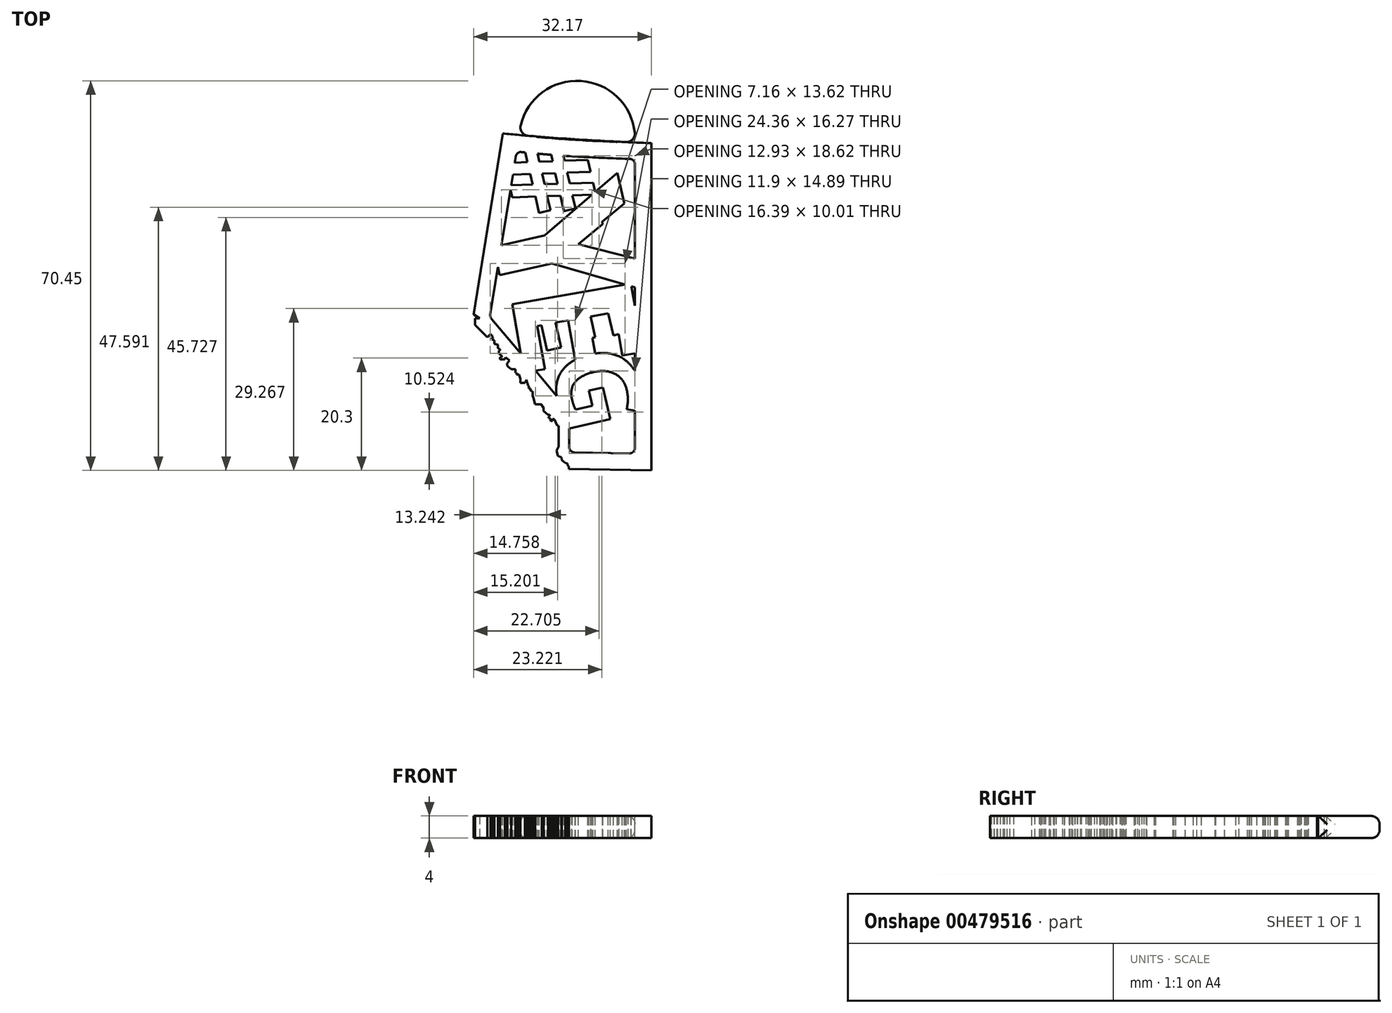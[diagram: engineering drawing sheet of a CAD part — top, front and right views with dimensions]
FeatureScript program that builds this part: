
annotation { "Feature Type Name" : "Feature", "Feature Type Description" : "" }
export const myFeature = defineFeature(function(context is Context, id is Id, definition is map)
    precondition{}
    {
        {
            var Q0;
            Q0=qCreatedBy(makeId("Top.planeOp"),FACE);
            var sketch = newSketch(context, id + "F0", { "sketchPlane" : qUnion([Q0])});
            skLineSegment(sketch, "E0", {"start": v(12.94, 76.8) * mm, "end": v(7.68, 44.1) * mm});
            skLineSegment(sketch, "E1", {"start": v(7.68, 44.1) * mm, "end": v(8.75, 43.35) * mm});
            skLineSegment(sketch, "E2", {"start": v(8.75, 43.35) * mm, "end": v(7.97, 43.35) * mm});
            skLineSegment(sketch, "E3", {"start": v(7.97, 43.35) * mm, "end": v(7.97, 42.17) * mm});
            skLineSegment(sketch, "E4", {"start": v(7.97, 42.17) * mm, "end": v(10.17, 39.93) * mm});
            skLineSegment(sketch, "E5", {"start": v(10.17, 39.93) * mm, "end": v(10.74, 40.49) * mm});
            skLineSegment(sketch, "E6", {"start": v(10.74, 40.49) * mm, "end": v(11.19, 40.03) * mm});
            skLineSegment(sketch, "E7", {"start": v(11.19, 40.03) * mm, "end": v(11, 39.57) * mm});
            skLineSegment(sketch, "E8", {"start": v(11, 39.57) * mm, "end": v(11.46, 39.39) * mm});
            skLineSegment(sketch, "E9", {"start": v(11.46, 39.39) * mm, "end": v(11.46, 38.73) * mm});
            skLineSegment(sketch, "E10", {"start": v(11.46, 38.73) * mm, "end": v(12.08, 38.61) * mm});
            skLineSegment(sketch, "E11", {"start": v(12.08, 38.61) * mm, "end": v(12.08, 37.96) * mm});
            skLineSegment(sketch, "E12", {"start": v(12.08, 37.96) * mm, "end": v(12.25, 37.87) * mm});
            skLineSegment(sketch, "E13", {"start": v(12.25, 37.87) * mm, "end": v(12.46, 37.8) * mm});
            skLineSegment(sketch, "E14", {"start": v(12.46, 37.8) * mm, "end": v(12.46, 37.52) * mm});
            skLineSegment(sketch, "E15", {"start": v(12.46, 37.52) * mm, "end": v(12.25, 37.52) * mm});
            skLineSegment(sketch, "E16", {"start": v(12.25, 37.52) * mm, "end": v(12.25, 36.96) * mm});
            skLineSegment(sketch, "E17", {"start": v(12.25, 36.96) * mm, "end": v(12.43, 36.93) * mm});
            skLineSegment(sketch, "E18", {"start": v(12.43, 36.93) * mm, "end": v(12.75, 36.55) * mm});
            skLineSegment(sketch, "E19", {"start": v(12.75, 36.55) * mm, "end": v(12.75, 36.3) * mm});
            skLineSegment(sketch, "E20", {"start": v(12.75, 36.3) * mm, "end": v(12.46, 36.3) * mm});
            skLineSegment(sketch, "E21", {"start": v(12.46, 36.3) * mm, "end": v(12.46, 35.94) * mm});
            skLineSegment(sketch, "E22", {"start": v(12.46, 35.94) * mm, "end": v(13.34, 35.94) * mm});
            skLineSegment(sketch, "E23", {"start": v(13.34, 35.94) * mm, "end": v(13.45, 36.34) * mm});
            skLineSegment(sketch, "E24", {"start": v(13.45, 36.34) * mm, "end": v(14.19, 35.72) * mm});
            skLineSegment(sketch, "E25", {"start": v(14.19, 35.72) * mm, "end": v(13.73, 35.19) * mm});
            skLineSegment(sketch, "E26", {"start": v(13.73, 35.19) * mm, "end": v(13.79, 34.75) * mm});
            skLineSegment(sketch, "E27", {"start": v(13.79, 34.75) * mm, "end": v(14.47, 34.2) * mm});
            skLineSegment(sketch, "E28", {"start": v(14.47, 34.2) * mm, "end": v(15.28, 34.2) * mm});
            skLineSegment(sketch, "E29", {"start": v(15.28, 34.2) * mm, "end": v(15.28, 33.54) * mm});
            skLineSegment(sketch, "E30", {"start": v(15.28, 33.54) * mm, "end": v(15.46, 33.54) * mm});
            skLineSegment(sketch, "E31", {"start": v(15.46, 33.54) * mm, "end": v(15.46, 33.22) * mm});
            skLineSegment(sketch, "E32", {"start": v(15.46, 33.22) * mm, "end": v(15.87, 33.22) * mm});
            skLineSegment(sketch, "E33", {"start": v(15.87, 33.22) * mm, "end": v(16.14, 32.43) * mm});
            skLineSegment(sketch, "E34", {"start": v(16.14, 32.43) * mm, "end": v(16.14, 31.7) * mm});
            skLineSegment(sketch, "E35", {"start": v(16.14, 31.7) * mm, "end": v(16.97, 31.7) * mm});
            skLineSegment(sketch, "E36", {"start": v(16.97, 31.7) * mm, "end": v(17.27, 32.23) * mm});
            skLineSegment(sketch, "E37", {"start": v(17.27, 32.23) * mm, "end": v(17.33, 31.74) * mm});
            skLineSegment(sketch, "E38", {"start": v(17.33, 31.74) * mm, "end": v(17.48, 31.65) * mm});
            skLineSegment(sketch, "E39", {"start": v(17.48, 31.65) * mm, "end": v(17.48, 31.25) * mm});
            skLineSegment(sketch, "E40", {"start": v(17.48, 31.25) * mm, "end": v(17.7, 31.18) * mm});
            skLineSegment(sketch, "E41", {"start": v(17.7, 31.18) * mm, "end": v(17.7, 30.7) * mm});
            skLineSegment(sketch, "E42", {"start": v(17.7, 30.7) * mm, "end": v(18.01, 30.66) * mm});
            skLineSegment(sketch, "E43", {"start": v(18.01, 30.66) * mm, "end": v(18.01, 30.29) * mm});
            skLineSegment(sketch, "E44", {"start": v(18.01, 30.29) * mm, "end": v(18.18, 30.2) * mm});
            skLineSegment(sketch, "E45", {"start": v(18.18, 30.2) * mm, "end": v(18.33, 30.17) * mm});
            skLineSegment(sketch, "E46", {"start": v(18.33, 30.17) * mm, "end": v(18.33, 29.33) * mm});
            skLineSegment(sketch, "E47", {"start": v(18.33, 29.33) * mm, "end": v(18.46, 29) * mm});
            skLineSegment(sketch, "E48", {"start": v(18.46, 29) * mm, "end": v(18.83, 27.8) * mm});
            skLineSegment(sketch, "E49", {"start": v(18.83, 27.8) * mm, "end": v(20, 27.8) * mm});
            skLineSegment(sketch, "E50", {"start": v(20, 27.8) * mm, "end": v(20, 27.5) * mm});
            skLineSegment(sketch, "E51", {"start": v(20, 27.5) * mm, "end": v(20.36, 27.3) * mm});
            skLineSegment(sketch, "E52", {"start": v(20.36, 27.3) * mm, "end": v(20.36, 26.6) * mm});
            skLineSegment(sketch, "E53", {"start": v(20.36, 26.6) * mm, "end": v(21.15, 25.9) * mm});
            skLineSegment(sketch, "E54", {"start": v(21.15, 25.9) * mm, "end": v(21.45, 25.9) * mm});
            skLineSegment(sketch, "E55", {"start": v(21.45, 25.9) * mm, "end": v(21.5, 25.75) * mm});
            skLineSegment(sketch, "E56", {"start": v(21.5, 25.75) * mm, "end": v(21.21, 25.6) * mm});
            skLineSegment(sketch, "E57", {"start": v(21.21, 25.6) * mm, "end": v(21.3, 25.31) * mm});
            skLineSegment(sketch, "E58", {"start": v(21.3, 25.31) * mm, "end": v(21.54, 25.28) * mm});
            skLineSegment(sketch, "E59", {"start": v(21.54, 25.28) * mm, "end": v(21.6, 24.78) * mm});
            skLineSegment(sketch, "E60", {"start": v(21.6, 24.78) * mm, "end": v(21.94, 24.82) * mm});
            skLineSegment(sketch, "E61", {"start": v(21.94, 24.82) * mm, "end": v(21.99, 25.2) * mm});
            skLineSegment(sketch, "E62", {"start": v(21.99, 25.2) * mm, "end": v(22.33, 25.1) * mm});
            skLineSegment(sketch, "E63", {"start": v(22.33, 25.1) * mm, "end": v(22.84, 23.96) * mm});
            skLineSegment(sketch, "E64", {"start": v(22.84, 23.96) * mm, "end": v(23.05, 23.94) * mm});
            skLineSegment(sketch, "E65", {"start": v(23.05, 23.94) * mm, "end": v(23.05, 22.88) * mm});
            skLineSegment(sketch, "E66", {"start": v(23.05, 22.88) * mm, "end": v(23.05, 20.17) * mm});
            skLineSegment(sketch, "E67", {"start": v(23.05, 20.17) * mm, "end": v(22.65, 19.46) * mm});
            skLineSegment(sketch, "E68", {"start": v(22.65, 19.46) * mm, "end": v(22.95, 18.48) * mm});
            skLineSegment(sketch, "E69", {"start": v(22.95, 18.48) * mm, "end": v(23.56, 18.23) * mm});
            skLineSegment(sketch, "E70", {"start": v(23.56, 18.23) * mm, "end": v(23.64, 17.74) * mm});
            skLineSegment(sketch, "E71", {"start": v(23.64, 17.74) * mm, "end": v(24.27, 17.22) * mm});
            skLineSegment(sketch, "E72", {"start": v(24.27, 17.22) * mm, "end": v(24.63, 17.14) * mm});
            skLineSegment(sketch, "E73", {"start": v(24.63, 17.14) * mm, "end": v(24.72, 16.67) * mm});
            skLineSegment(sketch, "E74", {"start": v(24.72, 16.67) * mm, "end": v(24.9, 16.57) * mm});
            skLineSegment(sketch, "E75", {"start": v(24.9, 16.57) * mm, "end": v(24.9, 16.14) * mm});
            skLineSegment(sketch, "E76", {"start": v(24.9, 16.14) * mm, "end": v(39.85, 15.87) * mm});
            skLineSegment(sketch, "E77", {"start": v(39.85, 15.87) * mm, "end": v(39.85, 75.04) * mm});
            skFitSpline(sketch, "E78", {"points": [v(12.94, 76.8) * mm, v(39.85, 75.04) * mm], "startDerivative": vector(26.48, -2.57) * mm, "endDerivative": vector(26.93, -1.05) * mm});
            skLineSegment(sketch, "E79.0", {"start": v(15.31, 72.63) * mm, "end": v(10.71, 44.07) * mm});
            skFitSpline(sketch, "E80.0", {"points": [v(12.65, 73.81) * mm, v(21.55, 72.95) * mm, v(30.71, 72.4) * mm, v(39.73, 72.04) * mm]});
            skLineSegment(sketch, "E81.0", {"start": v(25.93, 19.12) * mm, "end": v(35.83, 18.95) * mm});
            skLineSegment(sketch, "E82.trimOffspring", {"start": v(36.85, 19.95) * mm, "end": v(36.85, 71.2) * mm});
            skLineSegment(sketch, "E83", {"start": v(24.95, 20.12) * mm, "end": v(24.95, 26.3) * mm});
            skLineSegment(sketch, "E84", {"start": v(24.72, 26.95) * mm, "end": v(10.93, 43.26) * mm});
            skPoint(sketch, "E85.visualSharp", {"position": v(15.46, 73.55) * mm});
            skArc(sketch, "E85.filletArc", {"start": v(16.38, 73.47) * mm, "mid": v(15.68, 73.26) * mm, "end": v(15.31, 72.63) * mm});
            skPoint(sketch, "E86.visualSharp", {"position": v(36.85, 72.16) * mm});
            skArc(sketch, "E86.filletArc", {"start": v(36.85, 71.2) * mm, "mid": v(36.57, 71.9) * mm, "end": v(35.9, 72.2) * mm});
            skPoint(sketch, "E87.visualSharp", {"position": v(36.85, 18.93) * mm});
            skArc(sketch, "E87.filletArc", {"start": v(35.83, 18.95) * mm, "mid": v(36.55, 19.23) * mm, "end": v(36.85, 19.95) * mm});
            skPoint(sketch, "E88.visualSharp", {"position": v(24.95, 19.14) * mm});
            skArc(sketch, "E88.filletArc", {"start": v(24.95, 20.12) * mm, "mid": v(25.24, 19.42) * mm, "end": v(25.93, 19.12) * mm});
            skPoint(sketch, "E89.visualSharp", {"position": v(24.95, 26.67) * mm});
            skArc(sketch, "E89.filletArc", {"start": v(24.95, 26.3) * mm, "mid": v(24.9, 26.64) * mm, "end": v(24.72, 26.95) * mm});
            skPoint(sketch, "E90.visualSharp", {"position": v(10.64, 43.62) * mm});
            skArc(sketch, "E90.filletArc", {"start": v(10.71, 44.07) * mm, "mid": v(10.73, 43.64) * mm, "end": v(10.93, 43.26) * mm});
            skSolve(sketch);
        }
        {
            var Q0;
            Q0=makeQuery(id+"F0.imprint","IMPRINT",FACE,{"disambiguationData":[TD([[makeQuery(id+"F0.imprint","IMPRINT",EDGE,{"derivedFrom":sQuery(id+"F0.wireOp",EDGE,"E0")}),1.0]])]});
            extrude(context, id + "F1", {"entities" : qUnion([Q0]), "depth" : 4 * mm});
        }
        {
            var Q0;
            Q0=makeQuery(id+"F1.opExtrude","CAP_FACE",FACE,{"disambiguationData":[OSD([sQuery(id+"F0.wireOp",EDGE,"E0"),sQuery(id+"F0.wireOp",EDGE,"E1"),sQuery(id+"F0.wireOp",EDGE,"E2"),sQuery(id+"F0.wireOp",EDGE,"E3"),sQuery(id+"F0.wireOp",EDGE,"E4"),sQuery(id+"F0.wireOp",EDGE,"E5"),sQuery(id+"F0.wireOp",EDGE,"E6"),sQuery(id+"F0.wireOp",EDGE,"E7"),sQuery(id+"F0.wireOp",EDGE,"E8"),sQuery(id+"F0.wireOp",EDGE,"E9"),sQuery(id+"F0.wireOp",EDGE,"E10"),sQuery(id+"F0.wireOp",EDGE,"E11"),sQuery(id+"F0.wireOp",EDGE,"E12"),sQuery(id+"F0.wireOp",EDGE,"E13"),sQuery(id+"F0.wireOp",EDGE,"E14"),sQuery(id+"F0.wireOp",EDGE,"E15"),sQuery(id+"F0.wireOp",EDGE,"E16"),sQuery(id+"F0.wireOp",EDGE,"E17"),sQuery(id+"F0.wireOp",EDGE,"E18"),sQuery(id+"F0.wireOp",EDGE,"E19"),sQuery(id+"F0.wireOp",EDGE,"E20"),sQuery(id+"F0.wireOp",EDGE,"E21"),sQuery(id+"F0.wireOp",EDGE,"E22"),sQuery(id+"F0.wireOp",EDGE,"E23"),sQuery(id+"F0.wireOp",EDGE,"E24"),sQuery(id+"F0.wireOp",EDGE,"E25"),sQuery(id+"F0.wireOp",EDGE,"E26"),sQuery(id+"F0.wireOp",EDGE,"E27"),sQuery(id+"F0.wireOp",EDGE,"E28"),sQuery(id+"F0.wireOp",EDGE,"E29"),sQuery(id+"F0.wireOp",EDGE,"E30"),sQuery(id+"F0.wireOp",EDGE,"E31"),sQuery(id+"F0.wireOp",EDGE,"E32"),sQuery(id+"F0.wireOp",EDGE,"E33"),sQuery(id+"F0.wireOp",EDGE,"E34"),sQuery(id+"F0.wireOp",EDGE,"E35"),sQuery(id+"F0.wireOp",EDGE,"E36"),sQuery(id+"F0.wireOp",EDGE,"E37"),sQuery(id+"F0.wireOp",EDGE,"E38"),sQuery(id+"F0.wireOp",EDGE,"E39"),sQuery(id+"F0.wireOp",EDGE,"E40"),sQuery(id+"F0.wireOp",EDGE,"E41"),sQuery(id+"F0.wireOp",EDGE,"E42"),sQuery(id+"F0.wireOp",EDGE,"E43"),sQuery(id+"F0.wireOp",EDGE,"E44"),sQuery(id+"F0.wireOp",EDGE,"E45"),sQuery(id+"F0.wireOp",EDGE,"E46"),sQuery(id+"F0.wireOp",EDGE,"E47"),sQuery(id+"F0.wireOp",EDGE,"E48"),sQuery(id+"F0.wireOp",EDGE,"E49"),sQuery(id+"F0.wireOp",EDGE,"E50"),sQuery(id+"F0.wireOp",EDGE,"E51"),sQuery(id+"F0.wireOp",EDGE,"E52"),sQuery(id+"F0.wireOp",EDGE,"E53"),sQuery(id+"F0.wireOp",EDGE,"E54"),sQuery(id+"F0.wireOp",EDGE,"E55"),sQuery(id+"F0.wireOp",EDGE,"E56"),sQuery(id+"F0.wireOp",EDGE,"E57"),sQuery(id+"F0.wireOp",EDGE,"E58"),sQuery(id+"F0.wireOp",EDGE,"E59"),sQuery(id+"F0.wireOp",EDGE,"E60"),sQuery(id+"F0.wireOp",EDGE,"E61"),sQuery(id+"F0.wireOp",EDGE,"E62"),sQuery(id+"F0.wireOp",EDGE,"E63"),sQuery(id+"F0.wireOp",EDGE,"E64"),sQuery(id+"F0.wireOp",EDGE,"E65"),sQuery(id+"F0.wireOp",EDGE,"E66"),sQuery(id+"F0.wireOp",EDGE,"E67"),sQuery(id+"F0.wireOp",EDGE,"E68"),sQuery(id+"F0.wireOp",EDGE,"E69"),sQuery(id+"F0.wireOp",EDGE,"E70"),sQuery(id+"F0.wireOp",EDGE,"E71"),sQuery(id+"F0.wireOp",EDGE,"E72"),sQuery(id+"F0.wireOp",EDGE,"E73"),sQuery(id+"F0.wireOp",EDGE,"E74"),sQuery(id+"F0.wireOp",EDGE,"E75"),sQuery(id+"F0.wireOp",EDGE,"E76"),sQuery(id+"F0.wireOp",EDGE,"E77"),sQuery(id+"F0.wireOp",EDGE,"E78"),sQuery(id+"F0.wireOp",EDGE,"E79.0"),sQuery(id+"F0.wireOp",EDGE,"E80.0"),sQuery(id+"F0.wireOp",EDGE,"E81.0"),sQuery(id+"F0.wireOp",EDGE,"E82.trimOffspring"),sQuery(id+"F0.wireOp",EDGE,"E83"),sQuery(id+"F0.wireOp",EDGE,"E84"),sQuery(id+"F0.wireOp",EDGE,"E85.filletArc"),sQuery(id+"F0.wireOp",EDGE,"E86.filletArc"),sQuery(id+"F0.wireOp",EDGE,"E87.filletArc"),sQuery(id+"F0.wireOp",EDGE,"E88.filletArc"),sQuery(id+"F0.wireOp",EDGE,"E89.filletArc"),sQuery(id+"F0.wireOp",EDGE,"E90.filletArc")])],"isStart":false});
            var sketch = newSketch(context, id + "F2", { "sketchPlane" : qUnion([Q0])});
            skText(sketch, "E91", { "text": "#YEG", "fontName": "NotoSans-Bold.ttf"});
            const initialGuessF2  = {"E91": [0.01276, 0.07352, 0.22255, -0.97492, 0.015]};
            skSetInitialGuess(sketch, initialGuessF2);
            skSolve(sketch);
        }
        {
            var Q0;
            Q0=makeQuery(id+"F2.imprint","IMPRINT",FACE,{"disambiguationData":[TD([[makeQuery(id+"F2.imprint","IMPRINT",EDGE,{"derivedFrom":sQuery(id+"F2.wireOp",EDGE,"E91.sketch_text.stroke-0")}),-1.0]])]});
            var Q1;
            Q1=makeQuery(id+"F2.imprint","IMPRINT",FACE,{"disambiguationData":[TD([[makeQuery(id+"F2.imprint","IMPRINT",EDGE,{"derivedFrom":sQuery(id+"F2.wireOp",EDGE,"E91.sketch_text.stroke-32")}),-1.0]])]});
            var Q2;
            Q2=makeQuery(id+"F2.imprint","IMPRINT",FACE,{"disambiguationData":[TD([[makeQuery(id+"F2.imprint","IMPRINT",EDGE,{"derivedFrom":sQuery(id+"F2.wireOp",EDGE,"E91.sketch_text.stroke-41")}),-1.0]])]});
            var Q3;
            Q3=makeQuery(id+"F2.imprint","IMPRINT",FACE,{"disambiguationData":[TD([[makeQuery(id+"F2.imprint","IMPRINT",EDGE,{"derivedFrom":sQuery(id+"F2.wireOp",EDGE,"E91.sketch_text.stroke-53")}),-1.0]])]});
            var Q4;
            Q4=makeQuery(id+"F1.opExtrude","CAP_FACE",FACE,{"disambiguationData":[OSD([sQuery(id+"F0.wireOp",EDGE,"E0"),sQuery(id+"F0.wireOp",EDGE,"E1"),sQuery(id+"F0.wireOp",EDGE,"E2"),sQuery(id+"F0.wireOp",EDGE,"E3"),sQuery(id+"F0.wireOp",EDGE,"E4"),sQuery(id+"F0.wireOp",EDGE,"E5"),sQuery(id+"F0.wireOp",EDGE,"E6"),sQuery(id+"F0.wireOp",EDGE,"E7"),sQuery(id+"F0.wireOp",EDGE,"E8"),sQuery(id+"F0.wireOp",EDGE,"E9"),sQuery(id+"F0.wireOp",EDGE,"E10"),sQuery(id+"F0.wireOp",EDGE,"E11"),sQuery(id+"F0.wireOp",EDGE,"E12"),sQuery(id+"F0.wireOp",EDGE,"E13"),sQuery(id+"F0.wireOp",EDGE,"E14"),sQuery(id+"F0.wireOp",EDGE,"E15"),sQuery(id+"F0.wireOp",EDGE,"E16"),sQuery(id+"F0.wireOp",EDGE,"E17"),sQuery(id+"F0.wireOp",EDGE,"E18"),sQuery(id+"F0.wireOp",EDGE,"E19"),sQuery(id+"F0.wireOp",EDGE,"E20"),sQuery(id+"F0.wireOp",EDGE,"E21"),sQuery(id+"F0.wireOp",EDGE,"E22"),sQuery(id+"F0.wireOp",EDGE,"E23"),sQuery(id+"F0.wireOp",EDGE,"E24"),sQuery(id+"F0.wireOp",EDGE,"E25"),sQuery(id+"F0.wireOp",EDGE,"E26"),sQuery(id+"F0.wireOp",EDGE,"E27"),sQuery(id+"F0.wireOp",EDGE,"E28"),sQuery(id+"F0.wireOp",EDGE,"E29"),sQuery(id+"F0.wireOp",EDGE,"E30"),sQuery(id+"F0.wireOp",EDGE,"E31"),sQuery(id+"F0.wireOp",EDGE,"E32"),sQuery(id+"F0.wireOp",EDGE,"E33"),sQuery(id+"F0.wireOp",EDGE,"E34"),sQuery(id+"F0.wireOp",EDGE,"E35"),sQuery(id+"F0.wireOp",EDGE,"E36"),sQuery(id+"F0.wireOp",EDGE,"E37"),sQuery(id+"F0.wireOp",EDGE,"E38"),sQuery(id+"F0.wireOp",EDGE,"E39"),sQuery(id+"F0.wireOp",EDGE,"E40"),sQuery(id+"F0.wireOp",EDGE,"E41"),sQuery(id+"F0.wireOp",EDGE,"E42"),sQuery(id+"F0.wireOp",EDGE,"E43"),sQuery(id+"F0.wireOp",EDGE,"E44"),sQuery(id+"F0.wireOp",EDGE,"E45"),sQuery(id+"F0.wireOp",EDGE,"E46"),sQuery(id+"F0.wireOp",EDGE,"E47"),sQuery(id+"F0.wireOp",EDGE,"E48"),sQuery(id+"F0.wireOp",EDGE,"E49"),sQuery(id+"F0.wireOp",EDGE,"E50"),sQuery(id+"F0.wireOp",EDGE,"E51"),sQuery(id+"F0.wireOp",EDGE,"E52"),sQuery(id+"F0.wireOp",EDGE,"E53"),sQuery(id+"F0.wireOp",EDGE,"E54"),sQuery(id+"F0.wireOp",EDGE,"E55"),sQuery(id+"F0.wireOp",EDGE,"E56"),sQuery(id+"F0.wireOp",EDGE,"E57"),sQuery(id+"F0.wireOp",EDGE,"E58"),sQuery(id+"F0.wireOp",EDGE,"E59"),sQuery(id+"F0.wireOp",EDGE,"E60"),sQuery(id+"F0.wireOp",EDGE,"E61"),sQuery(id+"F0.wireOp",EDGE,"E62"),sQuery(id+"F0.wireOp",EDGE,"E63"),sQuery(id+"F0.wireOp",EDGE,"E64"),sQuery(id+"F0.wireOp",EDGE,"E65"),sQuery(id+"F0.wireOp",EDGE,"E66"),sQuery(id+"F0.wireOp",EDGE,"E67"),sQuery(id+"F0.wireOp",EDGE,"E68"),sQuery(id+"F0.wireOp",EDGE,"E69"),sQuery(id+"F0.wireOp",EDGE,"E70"),sQuery(id+"F0.wireOp",EDGE,"E71"),sQuery(id+"F0.wireOp",EDGE,"E72"),sQuery(id+"F0.wireOp",EDGE,"E73"),sQuery(id+"F0.wireOp",EDGE,"E74"),sQuery(id+"F0.wireOp",EDGE,"E75"),sQuery(id+"F0.wireOp",EDGE,"E76"),sQuery(id+"F0.wireOp",EDGE,"E77"),sQuery(id+"F0.wireOp",EDGE,"E78"),sQuery(id+"F0.wireOp",EDGE,"E79.0"),sQuery(id+"F0.wireOp",EDGE,"E80.0"),sQuery(id+"F0.wireOp",EDGE,"E81.0"),sQuery(id+"F0.wireOp",EDGE,"E82.trimOffspring"),sQuery(id+"F0.wireOp",EDGE,"E83"),sQuery(id+"F0.wireOp",EDGE,"E84"),sQuery(id+"F0.wireOp",EDGE,"E85.filletArc"),sQuery(id+"F0.wireOp",EDGE,"E86.filletArc"),sQuery(id+"F0.wireOp",EDGE,"E87.filletArc"),sQuery(id+"F0.wireOp",EDGE,"E88.filletArc"),sQuery(id+"F0.wireOp",EDGE,"E89.filletArc"),sQuery(id+"F0.wireOp",EDGE,"E90.filletArc")])],"isStart":true});
            extrude(context, id + "F3", {"entities" : qUnion([Q0, Q1, Q2, Q3]), "endBound" : BoundingType.UP_TO_SURFACE, "oppositeDirection" : true, "endBoundEntityFace" : qUnion([Q4]), "depth" : 25 * mm});
        }
        {
            var Q0;
            Q0=makeQuery(id+"F3.opExtrude","SWEPT_BODY",BODY,{"disambiguationData":[OSD([sQuery(id+"F0.wireOp",EDGE,"E79.0"),sQuery(id+"F0.wireOp",EDGE,"E80.0"),sQuery(id+"F2.wireOp",EDGE,"E91.sketch_text.stroke-0"),sQuery(id+"F2.wireOp",EDGE,"E91.sketch_text.stroke-1"),sQuery(id+"F2.wireOp",EDGE,"E91.sketch_text.stroke-2"),sQuery(id+"F2.wireOp",EDGE,"E91.sketch_text.stroke-3"),sQuery(id+"F2.wireOp",EDGE,"E91.sketch_text.stroke-4"),sQuery(id+"F2.wireOp",EDGE,"E91.sketch_text.stroke-5"),sQuery(id+"F2.wireOp",EDGE,"E91.sketch_text.stroke-6"),sQuery(id+"F2.wireOp",EDGE,"E91.sketch_text.stroke-7"),sQuery(id+"F2.wireOp",EDGE,"E91.sketch_text.stroke-8"),sQuery(id+"F2.wireOp",EDGE,"E91.sketch_text.stroke-10"),sQuery(id+"F2.wireOp",EDGE,"E91.sketch_text.stroke-11"),sQuery(id+"F2.wireOp",EDGE,"E91.sketch_text.stroke-13"),sQuery(id+"F2.wireOp",EDGE,"E91.sketch_text.stroke-14"),sQuery(id+"F2.wireOp",EDGE,"E91.sketch_text.stroke-15"),sQuery(id+"F2.wireOp",EDGE,"E91.sketch_text.stroke-17"),sQuery(id+"F2.wireOp",EDGE,"E91.sketch_text.stroke-18"),sQuery(id+"F2.wireOp",EDGE,"E91.sketch_text.stroke-19"),sQuery(id+"F2.wireOp",EDGE,"E91.sketch_text.stroke-20"),sQuery(id+"F2.wireOp",EDGE,"E91.sketch_text.stroke-21"),sQuery(id+"F2.wireOp",EDGE,"E91.sketch_text.stroke-22"),sQuery(id+"F2.wireOp",EDGE,"E91.sketch_text.stroke-23"),sQuery(id+"F2.wireOp",EDGE,"E91.sketch_text.stroke-24"),sQuery(id+"F2.wireOp",EDGE,"E91.sketch_text.stroke-25"),sQuery(id+"F2.wireOp",EDGE,"E91.sketch_text.stroke-26"),sQuery(id+"F2.wireOp",EDGE,"E91.sketch_text.stroke-27"),sQuery(id+"F2.wireOp",EDGE,"E91.sketch_text.stroke-28"),sQuery(id+"F2.wireOp",EDGE,"E91.sketch_text.stroke-29"),sQuery(id+"F2.wireOp",EDGE,"E91.sketch_text.stroke-30"),sQuery(id+"F2.wireOp",EDGE,"E91.sketch_text.stroke-31")])]});
            var Q1;
            Q1=makeQuery(id+"F1.opExtrude","SWEPT_BODY",BODY,{"disambiguationData":[OSD([sQuery(id+"F0.wireOp",EDGE,"E0"),sQuery(id+"F0.wireOp",EDGE,"E1"),sQuery(id+"F0.wireOp",EDGE,"E2"),sQuery(id+"F0.wireOp",EDGE,"E3"),sQuery(id+"F0.wireOp",EDGE,"E4"),sQuery(id+"F0.wireOp",EDGE,"E5"),sQuery(id+"F0.wireOp",EDGE,"E6"),sQuery(id+"F0.wireOp",EDGE,"E7"),sQuery(id+"F0.wireOp",EDGE,"E8"),sQuery(id+"F0.wireOp",EDGE,"E9"),sQuery(id+"F0.wireOp",EDGE,"E10"),sQuery(id+"F0.wireOp",EDGE,"E11"),sQuery(id+"F0.wireOp",EDGE,"E12"),sQuery(id+"F0.wireOp",EDGE,"E13"),sQuery(id+"F0.wireOp",EDGE,"E14"),sQuery(id+"F0.wireOp",EDGE,"E15"),sQuery(id+"F0.wireOp",EDGE,"E16"),sQuery(id+"F0.wireOp",EDGE,"E17"),sQuery(id+"F0.wireOp",EDGE,"E18"),sQuery(id+"F0.wireOp",EDGE,"E19"),sQuery(id+"F0.wireOp",EDGE,"E20"),sQuery(id+"F0.wireOp",EDGE,"E21"),sQuery(id+"F0.wireOp",EDGE,"E22"),sQuery(id+"F0.wireOp",EDGE,"E23"),sQuery(id+"F0.wireOp",EDGE,"E24"),sQuery(id+"F0.wireOp",EDGE,"E25"),sQuery(id+"F0.wireOp",EDGE,"E26"),sQuery(id+"F0.wireOp",EDGE,"E27"),sQuery(id+"F0.wireOp",EDGE,"E28"),sQuery(id+"F0.wireOp",EDGE,"E29"),sQuery(id+"F0.wireOp",EDGE,"E30"),sQuery(id+"F0.wireOp",EDGE,"E31"),sQuery(id+"F0.wireOp",EDGE,"E32"),sQuery(id+"F0.wireOp",EDGE,"E33"),sQuery(id+"F0.wireOp",EDGE,"E34"),sQuery(id+"F0.wireOp",EDGE,"E35"),sQuery(id+"F0.wireOp",EDGE,"E36"),sQuery(id+"F0.wireOp",EDGE,"E37"),sQuery(id+"F0.wireOp",EDGE,"E38"),sQuery(id+"F0.wireOp",EDGE,"E39"),sQuery(id+"F0.wireOp",EDGE,"E40"),sQuery(id+"F0.wireOp",EDGE,"E41"),sQuery(id+"F0.wireOp",EDGE,"E42"),sQuery(id+"F0.wireOp",EDGE,"E43"),sQuery(id+"F0.wireOp",EDGE,"E44"),sQuery(id+"F0.wireOp",EDGE,"E45"),sQuery(id+"F0.wireOp",EDGE,"E46"),sQuery(id+"F0.wireOp",EDGE,"E47"),sQuery(id+"F0.wireOp",EDGE,"E48"),sQuery(id+"F0.wireOp",EDGE,"E49"),sQuery(id+"F0.wireOp",EDGE,"E50"),sQuery(id+"F0.wireOp",EDGE,"E51"),sQuery(id+"F0.wireOp",EDGE,"E52"),sQuery(id+"F0.wireOp",EDGE,"E53"),sQuery(id+"F0.wireOp",EDGE,"E54"),sQuery(id+"F0.wireOp",EDGE,"E55"),sQuery(id+"F0.wireOp",EDGE,"E56"),sQuery(id+"F0.wireOp",EDGE,"E57"),sQuery(id+"F0.wireOp",EDGE,"E58"),sQuery(id+"F0.wireOp",EDGE,"E59"),sQuery(id+"F0.wireOp",EDGE,"E60"),sQuery(id+"F0.wireOp",EDGE,"E61"),sQuery(id+"F0.wireOp",EDGE,"E62"),sQuery(id+"F0.wireOp",EDGE,"E63"),sQuery(id+"F0.wireOp",EDGE,"E64"),sQuery(id+"F0.wireOp",EDGE,"E65"),sQuery(id+"F0.wireOp",EDGE,"E66"),sQuery(id+"F0.wireOp",EDGE,"E67"),sQuery(id+"F0.wireOp",EDGE,"E68"),sQuery(id+"F0.wireOp",EDGE,"E69"),sQuery(id+"F0.wireOp",EDGE,"E70"),sQuery(id+"F0.wireOp",EDGE,"E71"),sQuery(id+"F0.wireOp",EDGE,"E72"),sQuery(id+"F0.wireOp",EDGE,"E73"),sQuery(id+"F0.wireOp",EDGE,"E74"),sQuery(id+"F0.wireOp",EDGE,"E75"),sQuery(id+"F0.wireOp",EDGE,"E76"),sQuery(id+"F0.wireOp",EDGE,"E77"),sQuery(id+"F0.wireOp",EDGE,"E78"),sQuery(id+"F0.wireOp",EDGE,"E79.0"),sQuery(id+"F0.wireOp",EDGE,"E80.0"),sQuery(id+"F0.wireOp",EDGE,"E81.0"),sQuery(id+"F0.wireOp",EDGE,"E82.trimOffspring"),sQuery(id+"F0.wireOp",EDGE,"E83"),sQuery(id+"F0.wireOp",EDGE,"E84"),sQuery(id+"F0.wireOp",EDGE,"E85.filletArc"),sQuery(id+"F0.wireOp",EDGE,"E86.filletArc"),sQuery(id+"F0.wireOp",EDGE,"E87.filletArc"),sQuery(id+"F0.wireOp",EDGE,"E88.filletArc"),sQuery(id+"F0.wireOp",EDGE,"E89.filletArc"),sQuery(id+"F0.wireOp",EDGE,"E90.filletArc")])]});
            booleanBodies(context, id + "F4", {"operationType" : BooleanOperationType.UNION, "tools" : qUnion([Q0, Q1])});
        }
        {
            var Q0;
            Q0=makeQuery(id+"F3.opExtrude","SWEPT_BODY",BODY,{"disambiguationData":[OSD([sQuery(id+"F0.wireOp",EDGE,"E82.trimOffspring"),sQuery(id+"F0.wireOp",EDGE,"E83"),sQuery(id+"F0.wireOp",EDGE,"E84"),sQuery(id+"F0.wireOp",EDGE,"E89.filletArc"),sQuery(id+"F2.wireOp",EDGE,"E91.sketch_text.stroke-53"),sQuery(id+"F2.wireOp",EDGE,"E91.sketch_text.stroke-54"),sQuery(id+"F2.wireOp",EDGE,"E91.sketch_text.stroke-57"),sQuery(id+"F2.wireOp",EDGE,"E91.sketch_text.stroke-58"),sQuery(id+"F2.wireOp",EDGE,"E91.sketch_text.stroke-59"),sQuery(id+"F2.wireOp",EDGE,"E91.sketch_text.stroke-60"),sQuery(id+"F2.wireOp",EDGE,"E91.sketch_text.stroke-62"),sQuery(id+"F2.wireOp",EDGE,"E91.sketch_text.stroke-63"),sQuery(id+"F2.wireOp",EDGE,"E91.sketch_text.stroke-64"),sQuery(id+"F2.wireOp",EDGE,"E91.sketch_text.stroke-65"),sQuery(id+"F2.wireOp",EDGE,"E91.sketch_text.stroke-66"),sQuery(id+"F2.wireOp",EDGE,"E91.sketch_text.stroke-67"),sQuery(id+"F2.wireOp",EDGE,"E91.sketch_text.stroke-68"),sQuery(id+"F2.wireOp",EDGE,"E91.sketch_text.stroke-69"),sQuery(id+"F2.wireOp",EDGE,"E91.sketch_text.stroke-70"),sQuery(id+"F2.wireOp",EDGE,"E91.sketch_text.stroke-71")])]});
            var Q1;
            Q1=makeQuery(id+"F3.opExtrude","SWEPT_BODY",BODY,{"disambiguationData":[OSD([sQuery(id+"F0.wireOp",EDGE,"E79.0"),sQuery(id+"F0.wireOp",EDGE,"E80.0"),sQuery(id+"F2.wireOp",EDGE,"E91.sketch_text.stroke-0"),sQuery(id+"F2.wireOp",EDGE,"E91.sketch_text.stroke-1"),sQuery(id+"F2.wireOp",EDGE,"E91.sketch_text.stroke-2"),sQuery(id+"F2.wireOp",EDGE,"E91.sketch_text.stroke-3"),sQuery(id+"F2.wireOp",EDGE,"E91.sketch_text.stroke-4"),sQuery(id+"F2.wireOp",EDGE,"E91.sketch_text.stroke-5"),sQuery(id+"F2.wireOp",EDGE,"E91.sketch_text.stroke-6"),sQuery(id+"F2.wireOp",EDGE,"E91.sketch_text.stroke-7"),sQuery(id+"F2.wireOp",EDGE,"E91.sketch_text.stroke-8"),sQuery(id+"F2.wireOp",EDGE,"E91.sketch_text.stroke-10"),sQuery(id+"F2.wireOp",EDGE,"E91.sketch_text.stroke-11"),sQuery(id+"F2.wireOp",EDGE,"E91.sketch_text.stroke-13"),sQuery(id+"F2.wireOp",EDGE,"E91.sketch_text.stroke-14"),sQuery(id+"F2.wireOp",EDGE,"E91.sketch_text.stroke-15"),sQuery(id+"F2.wireOp",EDGE,"E91.sketch_text.stroke-17"),sQuery(id+"F2.wireOp",EDGE,"E91.sketch_text.stroke-18"),sQuery(id+"F2.wireOp",EDGE,"E91.sketch_text.stroke-19"),sQuery(id+"F2.wireOp",EDGE,"E91.sketch_text.stroke-20"),sQuery(id+"F2.wireOp",EDGE,"E91.sketch_text.stroke-21"),sQuery(id+"F2.wireOp",EDGE,"E91.sketch_text.stroke-22"),sQuery(id+"F2.wireOp",EDGE,"E91.sketch_text.stroke-23"),sQuery(id+"F2.wireOp",EDGE,"E91.sketch_text.stroke-24"),sQuery(id+"F2.wireOp",EDGE,"E91.sketch_text.stroke-25"),sQuery(id+"F2.wireOp",EDGE,"E91.sketch_text.stroke-26"),sQuery(id+"F2.wireOp",EDGE,"E91.sketch_text.stroke-27"),sQuery(id+"F2.wireOp",EDGE,"E91.sketch_text.stroke-28"),sQuery(id+"F2.wireOp",EDGE,"E91.sketch_text.stroke-29"),sQuery(id+"F2.wireOp",EDGE,"E91.sketch_text.stroke-30"),sQuery(id+"F2.wireOp",EDGE,"E91.sketch_text.stroke-31")])]});
            booleanBodies(context, id + "F5", {"operationType" : BooleanOperationType.UNION, "tools" : qUnion([Q0, Q1])});
        }
        {
            var Q0;
            Q0=makeQuery(id+"F3.opExtrude","SWEPT_FACE",FACE,{"disambiguationData":[OSD([sQuery(id+"F2.wireOp",EDGE,"E91.sketch_text.stroke-39")])]});
            var sketch = newSketch(context, id + "F6", { "sketchPlane" : qUnion([Q0])});
            skLineSegment(sketch, "E92.0.0", {"start": v(51.97, 4) * mm, "end": v(51.97, 0) * mm});
            skLineSegment(sketch, "E92.0.1", {"start": v(51.97, 0) * mm, "end": v(55.38, 0) * mm});
            skLineSegment(sketch, "E92.0.2", {"start": v(55.38, 0) * mm, "end": v(55.38, 4) * mm});
            skLineSegment(sketch, "E92.0.3", {"start": v(55.38, 4) * mm, "end": v(51.97, 4) * mm});
            skLineSegment(sketch, "E93.0", {"start": v(52.97, 3) * mm, "end": v(52.97, 1) * mm});
            skLineSegment(sketch, "E93.1", {"start": v(54.38, 3) * mm, "end": v(52.97, 3) * mm});
            skLineSegment(sketch, "E93.2", {"start": v(54.38, 1) * mm, "end": v(54.38, 3) * mm});
            skLineSegment(sketch, "E93.3", {"start": v(52.97, 1) * mm, "end": v(54.38, 1) * mm});
            skLineSegment(sketch, "E94", {"start": v(52.97, 1) * mm, "end": v(52.97, 0) * mm});
            skLineSegment(sketch, "E95", {"start": v(54.38, 1) * mm, "end": v(54.38, 0) * mm});
            skSolve(sketch);
        }
        {
            var Q0;
            Q0=makeQuery(id+"F6.imprint","IMPRINT",FACE,{"disambiguationData":[TD([[makeQuery(id+"F6.imprint","IMPRINT",EDGE,{"derivedFrom":sQuery(id+"F6.wireOp",EDGE,"E93.3")}),-1.0]])]});
            var Q1;
            {var subQ7=sQuery(id+"F0.wireOp",EDGE,"E86.filletArc");var subQ11=sQuery(id+"F0.wireOp",EDGE,"E82.trimOffspring");Q1=makeQuery(id+"F5.opBoolean","SPLIT",FACE,{"disambiguationData":[TD([makeQuery(id+"F1.opExtrude","SWEPT_FACE",FACE,{"disambiguationData":[OSD([subQ7])]})])],"derivedFrom":makeQuery(id+"F1.opExtrude","SWEPT_FACE",FACE,{"disambiguationData":[OSD([subQ11])]})});}
            extrude(context, id + "F7", {"entities" : qUnion([Q0]), "endBound" : BoundingType.UP_TO_SURFACE, "endBoundEntityFace" : qUnion([Q1]), "depth" : 25 * mm});
        }
        {
            var Q0;
            Q0=makeQuery(id+"F3.opExtrude","SWEPT_FACE",FACE,{"disambiguationData":[OSD([sQuery(id+"F2.wireOp",EDGE,"E91.sketch_text.stroke-33")])]});
            var sketch = newSketch(context, id + "F8", { "sketchPlane" : qUnion([Q0])});
            skLineSegment(sketch, "E96.0.0", {"start": v(42.38, 4) * mm, "end": v(42.38, 0) * mm});
            skLineSegment(sketch, "E96.0.1", {"start": v(42.38, 0) * mm, "end": v(45.78, 0) * mm});
            skLineSegment(sketch, "E96.0.2", {"start": v(45.78, 0) * mm, "end": v(45.78, 4) * mm});
            skLineSegment(sketch, "E96.0.3", {"start": v(45.78, 4) * mm, "end": v(42.38, 4) * mm});
            skLineSegment(sketch, "E97.0", {"start": v(43.38, 3) * mm, "end": v(43.38, 1) * mm});
            skLineSegment(sketch, "E97.1", {"start": v(44.78, 3) * mm, "end": v(43.38, 3) * mm});
            skLineSegment(sketch, "E97.2", {"start": v(44.78, 1) * mm, "end": v(44.78, 3) * mm});
            skLineSegment(sketch, "E97.3", {"start": v(43.38, 1) * mm, "end": v(44.78, 1) * mm});
            skLineSegment(sketch, "E98", {"start": v(43.38, 1) * mm, "end": v(43.38, 0) * mm});
            skLineSegment(sketch, "E99", {"start": v(44.78, 1) * mm, "end": v(44.78, 0) * mm});
            skSolve(sketch);
        }
        {
            var Q0;
            Q0=makeQuery(id+"F8.imprint","IMPRINT",FACE,{"disambiguationData":[TD([[makeQuery(id+"F8.imprint","IMPRINT",EDGE,{"derivedFrom":sQuery(id+"F8.wireOp",EDGE,"E97.3")}),-1.0]])]});
            var Q1;
            {var subQ7=sQuery(id+"F0.wireOp",EDGE,"E86.filletArc");var subQ11=sQuery(id+"F0.wireOp",EDGE,"E82.trimOffspring");Q1=makeQuery(id+"F5.opBoolean","SPLIT",FACE,{"disambiguationData":[TD([makeQuery(id+"F1.opExtrude","SWEPT_FACE",FACE,{"disambiguationData":[OSD([subQ7])]})])],"derivedFrom":makeQuery(id+"F1.opExtrude","SWEPT_FACE",FACE,{"disambiguationData":[OSD([subQ11])]})});}
            extrude(context, id + "F9", {"entities" : qUnion([Q0]), "endBound" : BoundingType.UP_TO_SURFACE, "endBoundEntityFace" : qUnion([Q1]), "depth" : 25 * mm});
        }
        {
            var Q0;
            Q0=makeQuery(id+"F3.opExtrude","SWEPT_FACE",FACE,{"disambiguationData":[OSD([sQuery(id+"F2.wireOp",EDGE,"E91.sketch_text.stroke-36")])]});
            var sketch = newSketch(context, id + "F10", { "sketchPlane" : qUnion([Q0])});
            skLineSegment(sketch, "E100.0.0", {"start": v(-50.45, 4) * mm, "end": v(-50.45, 0) * mm});
            skLineSegment(sketch, "E100.0.1", {"start": v(-50.45, 0) * mm, "end": v(-47.32, 0) * mm});
            skLineSegment(sketch, "E100.0.2", {"start": v(-47.32, 0) * mm, "end": v(-47.32, 4) * mm});
            skLineSegment(sketch, "E100.0.3", {"start": v(-47.32, 4) * mm, "end": v(-50.45, 4) * mm});
            skLineSegment(sketch, "E101.0", {"start": v(-49.45, 3) * mm, "end": v(-49.45, 1) * mm});
            skLineSegment(sketch, "E101.1", {"start": v(-48.32, 3) * mm, "end": v(-49.45, 3) * mm});
            skLineSegment(sketch, "E101.2", {"start": v(-48.32, 1) * mm, "end": v(-48.32, 3) * mm});
            skLineSegment(sketch, "E101.3", {"start": v(-49.45, 1) * mm, "end": v(-48.32, 1) * mm});
            skLineSegment(sketch, "E102", {"start": v(-49.45, 1) * mm, "end": v(-49.45, 0) * mm});
            skLineSegment(sketch, "E103", {"start": v(-48.32, 1) * mm, "end": v(-48.32, 0) * mm});
            skSolve(sketch);
        }
        {
            var Q0;
            Q0=makeQuery(id+"F10.imprint","IMPRINT",FACE,{"disambiguationData":[TD([[makeQuery(id+"F10.imprint","IMPRINT",EDGE,{"derivedFrom":sQuery(id+"F10.wireOp",EDGE,"E101.3")}),-1.0]])]});
            var Q1;
            {var subQ3=sQuery(id+"F0.wireOp",EDGE,"E79.0");var subQ4=sQuery(id+"F0.wireOp",EDGE,"E90.filletArc");Q1=makeQuery(id+"F4.opBoolean","SPLIT",FACE,{"disambiguationData":[TD([makeQuery(id+"F1.opExtrude","SWEPT_FACE",FACE,{"disambiguationData":[OSD([subQ4])]})])],"derivedFrom":makeQuery(id+"F1.opExtrude","SWEPT_FACE",FACE,{"disambiguationData":[OSD([subQ3])]})});}
            extrude(context, id + "F11", {"entities" : qUnion([Q0]), "endBound" : BoundingType.UP_TO_SURFACE, "endBoundEntityFace" : qUnion([Q1]), "depth" : 25 * mm});
        }
        {
            var Q0;
            Q0=makeQuery(id+"F11.opExtrude","SWEPT_BODY",BODY,{"disambiguationData":[OSD([sQuery(id+"F10.wireOp",EDGE,"E100.0.1"),sQuery(id+"F10.wireOp",EDGE,"E101.3"),sQuery(id+"F10.wireOp",EDGE,"E102"),sQuery(id+"F10.wireOp",EDGE,"E103")])]});
            var Q1;
            Q1=makeQuery(id+"F9.opExtrude","SWEPT_BODY",BODY,{"disambiguationData":[OSD([sQuery(id+"F8.wireOp",EDGE,"E96.0.1"),sQuery(id+"F8.wireOp",EDGE,"E97.3"),sQuery(id+"F8.wireOp",EDGE,"E98"),sQuery(id+"F8.wireOp",EDGE,"E99")])]});
            var Q2;
            Q2=makeQuery(id+"F7.opExtrude","SWEPT_BODY",BODY,{"disambiguationData":[OSD([sQuery(id+"F6.wireOp",EDGE,"E92.0.1"),sQuery(id+"F6.wireOp",EDGE,"E93.3"),sQuery(id+"F6.wireOp",EDGE,"E94"),sQuery(id+"F6.wireOp",EDGE,"E95")])]});
            deleteBodies(context, id + "F12", {"entities" : qUnion([Q0, Q1, Q2])});
        }
        {
            var Q0;
            {var subQ0=sQuery(id+"F0.wireOp",EDGE,"E80.0");var subQ1=sQuery(id+"F0.wireOp",EDGE,"E79.0");var subQ2=sQuery(id+"F0.wireOp",EDGE,"E89.filletArc");var subQ3=sQuery(id+"F0.wireOp",EDGE,"E84");var subQ4=sQuery(id+"F0.wireOp",EDGE,"E83");var subQ5=sQuery(id+"F0.wireOp",EDGE,"E82.trimOffspring");Q0=makeQuery(id+"F5.opBoolean","MERGE",FACE,{"derivedFrom":[makeQuery(id+"F3.opExtrude","CAP_FACE",FACE,{"disambiguationData":[OSD([subQ5,subQ4,subQ3,subQ2,sQuery(id+"F2.wireOp",EDGE,"E91.sketch_text.stroke-53"),sQuery(id+"F2.wireOp",EDGE,"E91.sketch_text.stroke-54"),sQuery(id+"F2.wireOp",EDGE,"E91.sketch_text.stroke-57"),sQuery(id+"F2.wireOp",EDGE,"E91.sketch_text.stroke-58"),sQuery(id+"F2.wireOp",EDGE,"E91.sketch_text.stroke-59"),sQuery(id+"F2.wireOp",EDGE,"E91.sketch_text.stroke-60"),sQuery(id+"F2.wireOp",EDGE,"E91.sketch_text.stroke-62"),sQuery(id+"F2.wireOp",EDGE,"E91.sketch_text.stroke-63"),sQuery(id+"F2.wireOp",EDGE,"E91.sketch_text.stroke-64"),sQuery(id+"F2.wireOp",EDGE,"E91.sketch_text.stroke-65"),sQuery(id+"F2.wireOp",EDGE,"E91.sketch_text.stroke-66"),sQuery(id+"F2.wireOp",EDGE,"E91.sketch_text.stroke-67"),sQuery(id+"F2.wireOp",EDGE,"E91.sketch_text.stroke-68"),sQuery(id+"F2.wireOp",EDGE,"E91.sketch_text.stroke-69"),sQuery(id+"F2.wireOp",EDGE,"E91.sketch_text.stroke-70"),sQuery(id+"F2.wireOp",EDGE,"E91.sketch_text.stroke-71")])],"isStart":true}),makeQuery(id+"F4.opBoolean","MERGE",FACE,{"derivedFrom":[makeQuery(id+"F1.opExtrude","CAP_FACE",FACE,{"disambiguationData":[OSD([sQuery(id+"F0.wireOp",EDGE,"E0"),sQuery(id+"F0.wireOp",EDGE,"E1"),sQuery(id+"F0.wireOp",EDGE,"E2"),sQuery(id+"F0.wireOp",EDGE,"E3"),sQuery(id+"F0.wireOp",EDGE,"E4"),sQuery(id+"F0.wireOp",EDGE,"E5"),sQuery(id+"F0.wireOp",EDGE,"E6"),sQuery(id+"F0.wireOp",EDGE,"E7"),sQuery(id+"F0.wireOp",EDGE,"E8"),sQuery(id+"F0.wireOp",EDGE,"E9"),sQuery(id+"F0.wireOp",EDGE,"E10"),sQuery(id+"F0.wireOp",EDGE,"E11"),sQuery(id+"F0.wireOp",EDGE,"E12"),sQuery(id+"F0.wireOp",EDGE,"E13"),sQuery(id+"F0.wireOp",EDGE,"E14"),sQuery(id+"F0.wireOp",EDGE,"E15"),sQuery(id+"F0.wireOp",EDGE,"E16"),sQuery(id+"F0.wireOp",EDGE,"E17"),sQuery(id+"F0.wireOp",EDGE,"E18"),sQuery(id+"F0.wireOp",EDGE,"E19"),sQuery(id+"F0.wireOp",EDGE,"E20"),sQuery(id+"F0.wireOp",EDGE,"E21"),sQuery(id+"F0.wireOp",EDGE,"E22"),sQuery(id+"F0.wireOp",EDGE,"E23"),sQuery(id+"F0.wireOp",EDGE,"E24"),sQuery(id+"F0.wireOp",EDGE,"E25"),sQuery(id+"F0.wireOp",EDGE,"E26"),sQuery(id+"F0.wireOp",EDGE,"E27"),sQuery(id+"F0.wireOp",EDGE,"E28"),sQuery(id+"F0.wireOp",EDGE,"E29"),sQuery(id+"F0.wireOp",EDGE,"E30"),sQuery(id+"F0.wireOp",EDGE,"E31"),sQuery(id+"F0.wireOp",EDGE,"E32"),sQuery(id+"F0.wireOp",EDGE,"E33"),sQuery(id+"F0.wireOp",EDGE,"E34"),sQuery(id+"F0.wireOp",EDGE,"E35"),sQuery(id+"F0.wireOp",EDGE,"E36"),sQuery(id+"F0.wireOp",EDGE,"E37"),sQuery(id+"F0.wireOp",EDGE,"E38"),sQuery(id+"F0.wireOp",EDGE,"E39"),sQuery(id+"F0.wireOp",EDGE,"E40"),sQuery(id+"F0.wireOp",EDGE,"E41"),sQuery(id+"F0.wireOp",EDGE,"E42"),sQuery(id+"F0.wireOp",EDGE,"E43"),sQuery(id+"F0.wireOp",EDGE,"E44"),sQuery(id+"F0.wireOp",EDGE,"E45"),sQuery(id+"F0.wireOp",EDGE,"E46"),sQuery(id+"F0.wireOp",EDGE,"E47"),sQuery(id+"F0.wireOp",EDGE,"E48"),sQuery(id+"F0.wireOp",EDGE,"E49"),sQuery(id+"F0.wireOp",EDGE,"E50"),sQuery(id+"F0.wireOp",EDGE,"E51"),sQuery(id+"F0.wireOp",EDGE,"E52"),sQuery(id+"F0.wireOp",EDGE,"E53"),sQuery(id+"F0.wireOp",EDGE,"E54"),sQuery(id+"F0.wireOp",EDGE,"E55"),sQuery(id+"F0.wireOp",EDGE,"E56"),sQuery(id+"F0.wireOp",EDGE,"E57"),sQuery(id+"F0.wireOp",EDGE,"E58"),sQuery(id+"F0.wireOp",EDGE,"E59"),sQuery(id+"F0.wireOp",EDGE,"E60"),sQuery(id+"F0.wireOp",EDGE,"E61"),sQuery(id+"F0.wireOp",EDGE,"E62"),sQuery(id+"F0.wireOp",EDGE,"E63"),sQuery(id+"F0.wireOp",EDGE,"E64"),sQuery(id+"F0.wireOp",EDGE,"E65"),sQuery(id+"F0.wireOp",EDGE,"E66"),sQuery(id+"F0.wireOp",EDGE,"E67"),sQuery(id+"F0.wireOp",EDGE,"E68"),sQuery(id+"F0.wireOp",EDGE,"E69"),sQuery(id+"F0.wireOp",EDGE,"E70"),sQuery(id+"F0.wireOp",EDGE,"E71"),sQuery(id+"F0.wireOp",EDGE,"E72"),sQuery(id+"F0.wireOp",EDGE,"E73"),sQuery(id+"F0.wireOp",EDGE,"E74"),sQuery(id+"F0.wireOp",EDGE,"E75"),sQuery(id+"F0.wireOp",EDGE,"E76"),sQuery(id+"F0.wireOp",EDGE,"E77"),sQuery(id+"F0.wireOp",EDGE,"E78"),subQ1,subQ0,sQuery(id+"F0.wireOp",EDGE,"E81.0"),subQ5,subQ4,subQ3,sQuery(id+"F0.wireOp",EDGE,"E85.filletArc"),sQuery(id+"F0.wireOp",EDGE,"E86.filletArc"),sQuery(id+"F0.wireOp",EDGE,"E87.filletArc"),sQuery(id+"F0.wireOp",EDGE,"E88.filletArc"),subQ2,sQuery(id+"F0.wireOp",EDGE,"E90.filletArc")])],"isStart":false}),makeQuery(id+"F3.opExtrude","CAP_FACE",FACE,{"disambiguationData":[OSD([subQ1,subQ0,sQuery(id+"F2.wireOp",EDGE,"E91.sketch_text.stroke-0"),sQuery(id+"F2.wireOp",EDGE,"E91.sketch_text.stroke-1"),sQuery(id+"F2.wireOp",EDGE,"E91.sketch_text.stroke-2"),sQuery(id+"F2.wireOp",EDGE,"E91.sketch_text.stroke-3"),sQuery(id+"F2.wireOp",EDGE,"E91.sketch_text.stroke-4"),sQuery(id+"F2.wireOp",EDGE,"E91.sketch_text.stroke-5"),sQuery(id+"F2.wireOp",EDGE,"E91.sketch_text.stroke-6"),sQuery(id+"F2.wireOp",EDGE,"E91.sketch_text.stroke-7"),sQuery(id+"F2.wireOp",EDGE,"E91.sketch_text.stroke-8"),sQuery(id+"F2.wireOp",EDGE,"E91.sketch_text.stroke-10"),sQuery(id+"F2.wireOp",EDGE,"E91.sketch_text.stroke-11"),sQuery(id+"F2.wireOp",EDGE,"E91.sketch_text.stroke-13"),sQuery(id+"F2.wireOp",EDGE,"E91.sketch_text.stroke-14"),sQuery(id+"F2.wireOp",EDGE,"E91.sketch_text.stroke-15"),sQuery(id+"F2.wireOp",EDGE,"E91.sketch_text.stroke-17"),sQuery(id+"F2.wireOp",EDGE,"E91.sketch_text.stroke-18"),sQuery(id+"F2.wireOp",EDGE,"E91.sketch_text.stroke-19"),sQuery(id+"F2.wireOp",EDGE,"E91.sketch_text.stroke-20"),sQuery(id+"F2.wireOp",EDGE,"E91.sketch_text.stroke-21"),sQuery(id+"F2.wireOp",EDGE,"E91.sketch_text.stroke-22"),sQuery(id+"F2.wireOp",EDGE,"E91.sketch_text.stroke-23"),sQuery(id+"F2.wireOp",EDGE,"E91.sketch_text.stroke-24"),sQuery(id+"F2.wireOp",EDGE,"E91.sketch_text.stroke-25"),sQuery(id+"F2.wireOp",EDGE,"E91.sketch_text.stroke-26"),sQuery(id+"F2.wireOp",EDGE,"E91.sketch_text.stroke-27"),sQuery(id+"F2.wireOp",EDGE,"E91.sketch_text.stroke-28"),sQuery(id+"F2.wireOp",EDGE,"E91.sketch_text.stroke-29"),sQuery(id+"F2.wireOp",EDGE,"E91.sketch_text.stroke-30"),sQuery(id+"F2.wireOp",EDGE,"E91.sketch_text.stroke-31")])],"isStart":true})]})]});}
            var sketch = newSketch(context, id + "F13", { "sketchPlane" : qUnion([Q0])});
            skText(sketch, "E104", { "text": "Y", "fontName": "NotoSans-Bold.ttf"});
            const initialGuessF13  = {"E104": [0.0095, 0.0643, 0.2174, -0.97608, 0.025]};
            skSetInitialGuess(sketch, initialGuessF13);
            skSolve(sketch);
        }
        {
            var Q0;
            {var subQ29=sQuery(id+"F13.wireOp",EDGE,"E104.sketch_text.stroke-3");Q0=makeQuery(id+"F13.imprint","IMPRINT",FACE,{"disambiguationData":[TD([[makeQuery(id+"F13.imprint","IMPRINT",EDGE,{"derivedFrom":subQ29}),-1.0]])]});}
            var Q1;
            {var subQ0=sQuery(id+"F0.wireOp",EDGE,"E80.0");var subQ1=sQuery(id+"F0.wireOp",EDGE,"E79.0");var subQ2=sQuery(id+"F0.wireOp",EDGE,"E89.filletArc");var subQ3=sQuery(id+"F0.wireOp",EDGE,"E84");var subQ4=sQuery(id+"F0.wireOp",EDGE,"E83");var subQ5=sQuery(id+"F0.wireOp",EDGE,"E82.trimOffspring");Q1=makeQuery(id+"F5.opBoolean","MERGE",FACE,{"derivedFrom":[makeQuery(id+"F3.opExtrude","CAP_FACE",FACE,{"disambiguationData":[OSD([subQ5,subQ4,subQ3,subQ2,sQuery(id+"F2.wireOp",EDGE,"E91.sketch_text.stroke-53"),sQuery(id+"F2.wireOp",EDGE,"E91.sketch_text.stroke-54"),sQuery(id+"F2.wireOp",EDGE,"E91.sketch_text.stroke-57"),sQuery(id+"F2.wireOp",EDGE,"E91.sketch_text.stroke-58"),sQuery(id+"F2.wireOp",EDGE,"E91.sketch_text.stroke-59"),sQuery(id+"F2.wireOp",EDGE,"E91.sketch_text.stroke-60"),sQuery(id+"F2.wireOp",EDGE,"E91.sketch_text.stroke-62"),sQuery(id+"F2.wireOp",EDGE,"E91.sketch_text.stroke-63"),sQuery(id+"F2.wireOp",EDGE,"E91.sketch_text.stroke-64"),sQuery(id+"F2.wireOp",EDGE,"E91.sketch_text.stroke-65"),sQuery(id+"F2.wireOp",EDGE,"E91.sketch_text.stroke-66"),sQuery(id+"F2.wireOp",EDGE,"E91.sketch_text.stroke-67"),sQuery(id+"F2.wireOp",EDGE,"E91.sketch_text.stroke-68"),sQuery(id+"F2.wireOp",EDGE,"E91.sketch_text.stroke-69"),sQuery(id+"F2.wireOp",EDGE,"E91.sketch_text.stroke-70"),sQuery(id+"F2.wireOp",EDGE,"E91.sketch_text.stroke-71")])],"isStart":false}),makeQuery(id+"F4.opBoolean","MERGE",FACE,{"derivedFrom":[makeQuery(id+"F1.opExtrude","CAP_FACE",FACE,{"disambiguationData":[OSD([sQuery(id+"F0.wireOp",EDGE,"E0"),sQuery(id+"F0.wireOp",EDGE,"E1"),sQuery(id+"F0.wireOp",EDGE,"E2"),sQuery(id+"F0.wireOp",EDGE,"E3"),sQuery(id+"F0.wireOp",EDGE,"E4"),sQuery(id+"F0.wireOp",EDGE,"E5"),sQuery(id+"F0.wireOp",EDGE,"E6"),sQuery(id+"F0.wireOp",EDGE,"E7"),sQuery(id+"F0.wireOp",EDGE,"E8"),sQuery(id+"F0.wireOp",EDGE,"E9"),sQuery(id+"F0.wireOp",EDGE,"E10"),sQuery(id+"F0.wireOp",EDGE,"E11"),sQuery(id+"F0.wireOp",EDGE,"E12"),sQuery(id+"F0.wireOp",EDGE,"E13"),sQuery(id+"F0.wireOp",EDGE,"E14"),sQuery(id+"F0.wireOp",EDGE,"E15"),sQuery(id+"F0.wireOp",EDGE,"E16"),sQuery(id+"F0.wireOp",EDGE,"E17"),sQuery(id+"F0.wireOp",EDGE,"E18"),sQuery(id+"F0.wireOp",EDGE,"E19"),sQuery(id+"F0.wireOp",EDGE,"E20"),sQuery(id+"F0.wireOp",EDGE,"E21"),sQuery(id+"F0.wireOp",EDGE,"E22"),sQuery(id+"F0.wireOp",EDGE,"E23"),sQuery(id+"F0.wireOp",EDGE,"E24"),sQuery(id+"F0.wireOp",EDGE,"E25"),sQuery(id+"F0.wireOp",EDGE,"E26"),sQuery(id+"F0.wireOp",EDGE,"E27"),sQuery(id+"F0.wireOp",EDGE,"E28"),sQuery(id+"F0.wireOp",EDGE,"E29"),sQuery(id+"F0.wireOp",EDGE,"E30"),sQuery(id+"F0.wireOp",EDGE,"E31"),sQuery(id+"F0.wireOp",EDGE,"E32"),sQuery(id+"F0.wireOp",EDGE,"E33"),sQuery(id+"F0.wireOp",EDGE,"E34"),sQuery(id+"F0.wireOp",EDGE,"E35"),sQuery(id+"F0.wireOp",EDGE,"E36"),sQuery(id+"F0.wireOp",EDGE,"E37"),sQuery(id+"F0.wireOp",EDGE,"E38"),sQuery(id+"F0.wireOp",EDGE,"E39"),sQuery(id+"F0.wireOp",EDGE,"E40"),sQuery(id+"F0.wireOp",EDGE,"E41"),sQuery(id+"F0.wireOp",EDGE,"E42"),sQuery(id+"F0.wireOp",EDGE,"E43"),sQuery(id+"F0.wireOp",EDGE,"E44"),sQuery(id+"F0.wireOp",EDGE,"E45"),sQuery(id+"F0.wireOp",EDGE,"E46"),sQuery(id+"F0.wireOp",EDGE,"E47"),sQuery(id+"F0.wireOp",EDGE,"E48"),sQuery(id+"F0.wireOp",EDGE,"E49"),sQuery(id+"F0.wireOp",EDGE,"E50"),sQuery(id+"F0.wireOp",EDGE,"E51"),sQuery(id+"F0.wireOp",EDGE,"E52"),sQuery(id+"F0.wireOp",EDGE,"E53"),sQuery(id+"F0.wireOp",EDGE,"E54"),sQuery(id+"F0.wireOp",EDGE,"E55"),sQuery(id+"F0.wireOp",EDGE,"E56"),sQuery(id+"F0.wireOp",EDGE,"E57"),sQuery(id+"F0.wireOp",EDGE,"E58"),sQuery(id+"F0.wireOp",EDGE,"E59"),sQuery(id+"F0.wireOp",EDGE,"E60"),sQuery(id+"F0.wireOp",EDGE,"E61"),sQuery(id+"F0.wireOp",EDGE,"E62"),sQuery(id+"F0.wireOp",EDGE,"E63"),sQuery(id+"F0.wireOp",EDGE,"E64"),sQuery(id+"F0.wireOp",EDGE,"E65"),sQuery(id+"F0.wireOp",EDGE,"E66"),sQuery(id+"F0.wireOp",EDGE,"E67"),sQuery(id+"F0.wireOp",EDGE,"E68"),sQuery(id+"F0.wireOp",EDGE,"E69"),sQuery(id+"F0.wireOp",EDGE,"E70"),sQuery(id+"F0.wireOp",EDGE,"E71"),sQuery(id+"F0.wireOp",EDGE,"E72"),sQuery(id+"F0.wireOp",EDGE,"E73"),sQuery(id+"F0.wireOp",EDGE,"E74"),sQuery(id+"F0.wireOp",EDGE,"E75"),sQuery(id+"F0.wireOp",EDGE,"E76"),sQuery(id+"F0.wireOp",EDGE,"E77"),sQuery(id+"F0.wireOp",EDGE,"E78"),subQ1,subQ0,sQuery(id+"F0.wireOp",EDGE,"E81.0"),subQ5,subQ4,subQ3,sQuery(id+"F0.wireOp",EDGE,"E85.filletArc"),sQuery(id+"F0.wireOp",EDGE,"E86.filletArc"),sQuery(id+"F0.wireOp",EDGE,"E87.filletArc"),sQuery(id+"F0.wireOp",EDGE,"E88.filletArc"),subQ2,sQuery(id+"F0.wireOp",EDGE,"E90.filletArc")])],"isStart":true}),makeQuery(id+"F3.opExtrude","CAP_FACE",FACE,{"disambiguationData":[OSD([subQ1,subQ0,sQuery(id+"F2.wireOp",EDGE,"E91.sketch_text.stroke-0"),sQuery(id+"F2.wireOp",EDGE,"E91.sketch_text.stroke-1"),sQuery(id+"F2.wireOp",EDGE,"E91.sketch_text.stroke-2"),sQuery(id+"F2.wireOp",EDGE,"E91.sketch_text.stroke-3"),sQuery(id+"F2.wireOp",EDGE,"E91.sketch_text.stroke-4"),sQuery(id+"F2.wireOp",EDGE,"E91.sketch_text.stroke-5"),sQuery(id+"F2.wireOp",EDGE,"E91.sketch_text.stroke-6"),sQuery(id+"F2.wireOp",EDGE,"E91.sketch_text.stroke-7"),sQuery(id+"F2.wireOp",EDGE,"E91.sketch_text.stroke-8"),sQuery(id+"F2.wireOp",EDGE,"E91.sketch_text.stroke-10"),sQuery(id+"F2.wireOp",EDGE,"E91.sketch_text.stroke-11"),sQuery(id+"F2.wireOp",EDGE,"E91.sketch_text.stroke-13"),sQuery(id+"F2.wireOp",EDGE,"E91.sketch_text.stroke-14"),sQuery(id+"F2.wireOp",EDGE,"E91.sketch_text.stroke-15"),sQuery(id+"F2.wireOp",EDGE,"E91.sketch_text.stroke-17"),sQuery(id+"F2.wireOp",EDGE,"E91.sketch_text.stroke-18"),sQuery(id+"F2.wireOp",EDGE,"E91.sketch_text.stroke-19"),sQuery(id+"F2.wireOp",EDGE,"E91.sketch_text.stroke-20"),sQuery(id+"F2.wireOp",EDGE,"E91.sketch_text.stroke-21"),sQuery(id+"F2.wireOp",EDGE,"E91.sketch_text.stroke-22"),sQuery(id+"F2.wireOp",EDGE,"E91.sketch_text.stroke-23"),sQuery(id+"F2.wireOp",EDGE,"E91.sketch_text.stroke-24"),sQuery(id+"F2.wireOp",EDGE,"E91.sketch_text.stroke-25"),sQuery(id+"F2.wireOp",EDGE,"E91.sketch_text.stroke-26"),sQuery(id+"F2.wireOp",EDGE,"E91.sketch_text.stroke-27"),sQuery(id+"F2.wireOp",EDGE,"E91.sketch_text.stroke-28"),sQuery(id+"F2.wireOp",EDGE,"E91.sketch_text.stroke-29"),sQuery(id+"F2.wireOp",EDGE,"E91.sketch_text.stroke-30"),sQuery(id+"F2.wireOp",EDGE,"E91.sketch_text.stroke-31")])],"isStart":false})]})]});}
            extrude(context, id + "F14", {"entities" : qUnion([Q0]), "operationType" : NewBodyOperationType.ADD, "endBound" : BoundingType.UP_TO_SURFACE, "oppositeDirection" : true, "endBoundEntityFace" : qUnion([Q1]), "depth" : 25 * mm});
        }
        {
            var Q0;
            {var subQ0=sQuery(id+"F2.wireOp",EDGE,"E91.sketch_text.stroke-24");var subQ1=sQuery(id+"F2.wireOp",EDGE,"E91.sketch_text.stroke-23");var subQ2=sQuery(id+"F0.wireOp",EDGE,"E82.trimOffspring");var subQ3=sQuery(id+"F0.wireOp",EDGE,"E79.0");var subQ4=sQuery(id+"F0.wireOp",EDGE,"E80.0");var subQ5=sQuery(id+"F0.wireOp",EDGE,"E89.filletArc");var subQ6=sQuery(id+"F0.wireOp",EDGE,"E84");var subQ7=sQuery(id+"F0.wireOp",EDGE,"E83");Q0=makeQuery(id+"F14.boolean.opBoolean","MERGE",FACE,{"derivedFrom":[makeQuery(id+"F5.opBoolean","MERGE",FACE,{"derivedFrom":[makeQuery(id+"F3.opExtrude","CAP_FACE",FACE,{"disambiguationData":[OSD([subQ2,subQ7,subQ6,subQ5,sQuery(id+"F2.wireOp",EDGE,"E91.sketch_text.stroke-53"),sQuery(id+"F2.wireOp",EDGE,"E91.sketch_text.stroke-54"),sQuery(id+"F2.wireOp",EDGE,"E91.sketch_text.stroke-57"),sQuery(id+"F2.wireOp",EDGE,"E91.sketch_text.stroke-58"),sQuery(id+"F2.wireOp",EDGE,"E91.sketch_text.stroke-59"),sQuery(id+"F2.wireOp",EDGE,"E91.sketch_text.stroke-60"),sQuery(id+"F2.wireOp",EDGE,"E91.sketch_text.stroke-62"),sQuery(id+"F2.wireOp",EDGE,"E91.sketch_text.stroke-63"),sQuery(id+"F2.wireOp",EDGE,"E91.sketch_text.stroke-64"),sQuery(id+"F2.wireOp",EDGE,"E91.sketch_text.stroke-65"),sQuery(id+"F2.wireOp",EDGE,"E91.sketch_text.stroke-66"),sQuery(id+"F2.wireOp",EDGE,"E91.sketch_text.stroke-67"),sQuery(id+"F2.wireOp",EDGE,"E91.sketch_text.stroke-68"),sQuery(id+"F2.wireOp",EDGE,"E91.sketch_text.stroke-69"),sQuery(id+"F2.wireOp",EDGE,"E91.sketch_text.stroke-70"),sQuery(id+"F2.wireOp",EDGE,"E91.sketch_text.stroke-71")])],"isStart":true}),makeQuery(id+"F4.opBoolean","MERGE",FACE,{"derivedFrom":[makeQuery(id+"F1.opExtrude","CAP_FACE",FACE,{"disambiguationData":[OSD([sQuery(id+"F0.wireOp",EDGE,"E0"),sQuery(id+"F0.wireOp",EDGE,"E1"),sQuery(id+"F0.wireOp",EDGE,"E2"),sQuery(id+"F0.wireOp",EDGE,"E3"),sQuery(id+"F0.wireOp",EDGE,"E4"),sQuery(id+"F0.wireOp",EDGE,"E5"),sQuery(id+"F0.wireOp",EDGE,"E6"),sQuery(id+"F0.wireOp",EDGE,"E7"),sQuery(id+"F0.wireOp",EDGE,"E8"),sQuery(id+"F0.wireOp",EDGE,"E9"),sQuery(id+"F0.wireOp",EDGE,"E10"),sQuery(id+"F0.wireOp",EDGE,"E11"),sQuery(id+"F0.wireOp",EDGE,"E12"),sQuery(id+"F0.wireOp",EDGE,"E13"),sQuery(id+"F0.wireOp",EDGE,"E14"),sQuery(id+"F0.wireOp",EDGE,"E15"),sQuery(id+"F0.wireOp",EDGE,"E16"),sQuery(id+"F0.wireOp",EDGE,"E17"),sQuery(id+"F0.wireOp",EDGE,"E18"),sQuery(id+"F0.wireOp",EDGE,"E19"),sQuery(id+"F0.wireOp",EDGE,"E20"),sQuery(id+"F0.wireOp",EDGE,"E21"),sQuery(id+"F0.wireOp",EDGE,"E22"),sQuery(id+"F0.wireOp",EDGE,"E23"),sQuery(id+"F0.wireOp",EDGE,"E24"),sQuery(id+"F0.wireOp",EDGE,"E25"),sQuery(id+"F0.wireOp",EDGE,"E26"),sQuery(id+"F0.wireOp",EDGE,"E27"),sQuery(id+"F0.wireOp",EDGE,"E28"),sQuery(id+"F0.wireOp",EDGE,"E29"),sQuery(id+"F0.wireOp",EDGE,"E30"),sQuery(id+"F0.wireOp",EDGE,"E31"),sQuery(id+"F0.wireOp",EDGE,"E32"),sQuery(id+"F0.wireOp",EDGE,"E33"),sQuery(id+"F0.wireOp",EDGE,"E34"),sQuery(id+"F0.wireOp",EDGE,"E35"),sQuery(id+"F0.wireOp",EDGE,"E36"),sQuery(id+"F0.wireOp",EDGE,"E37"),sQuery(id+"F0.wireOp",EDGE,"E38"),sQuery(id+"F0.wireOp",EDGE,"E39"),sQuery(id+"F0.wireOp",EDGE,"E40"),sQuery(id+"F0.wireOp",EDGE,"E41"),sQuery(id+"F0.wireOp",EDGE,"E42"),sQuery(id+"F0.wireOp",EDGE,"E43"),sQuery(id+"F0.wireOp",EDGE,"E44"),sQuery(id+"F0.wireOp",EDGE,"E45"),sQuery(id+"F0.wireOp",EDGE,"E46"),sQuery(id+"F0.wireOp",EDGE,"E47"),sQuery(id+"F0.wireOp",EDGE,"E48"),sQuery(id+"F0.wireOp",EDGE,"E49"),sQuery(id+"F0.wireOp",EDGE,"E50"),sQuery(id+"F0.wireOp",EDGE,"E51"),sQuery(id+"F0.wireOp",EDGE,"E52"),sQuery(id+"F0.wireOp",EDGE,"E53"),sQuery(id+"F0.wireOp",EDGE,"E54"),sQuery(id+"F0.wireOp",EDGE,"E55"),sQuery(id+"F0.wireOp",EDGE,"E56"),sQuery(id+"F0.wireOp",EDGE,"E57"),sQuery(id+"F0.wireOp",EDGE,"E58"),sQuery(id+"F0.wireOp",EDGE,"E59"),sQuery(id+"F0.wireOp",EDGE,"E60"),sQuery(id+"F0.wireOp",EDGE,"E61"),sQuery(id+"F0.wireOp",EDGE,"E62"),sQuery(id+"F0.wireOp",EDGE,"E63"),sQuery(id+"F0.wireOp",EDGE,"E64"),sQuery(id+"F0.wireOp",EDGE,"E65"),sQuery(id+"F0.wireOp",EDGE,"E66"),sQuery(id+"F0.wireOp",EDGE,"E67"),sQuery(id+"F0.wireOp",EDGE,"E68"),sQuery(id+"F0.wireOp",EDGE,"E69"),sQuery(id+"F0.wireOp",EDGE,"E70"),sQuery(id+"F0.wireOp",EDGE,"E71"),sQuery(id+"F0.wireOp",EDGE,"E72"),sQuery(id+"F0.wireOp",EDGE,"E73"),sQuery(id+"F0.wireOp",EDGE,"E74"),sQuery(id+"F0.wireOp",EDGE,"E75"),sQuery(id+"F0.wireOp",EDGE,"E76"),sQuery(id+"F0.wireOp",EDGE,"E77"),sQuery(id+"F0.wireOp",EDGE,"E78"),subQ3,subQ4,sQuery(id+"F0.wireOp",EDGE,"E81.0"),subQ2,subQ7,subQ6,sQuery(id+"F0.wireOp",EDGE,"E85.filletArc"),sQuery(id+"F0.wireOp",EDGE,"E86.filletArc"),sQuery(id+"F0.wireOp",EDGE,"E87.filletArc"),sQuery(id+"F0.wireOp",EDGE,"E88.filletArc"),subQ5,sQuery(id+"F0.wireOp",EDGE,"E90.filletArc")])],"isStart":false}),makeQuery(id+"F3.opExtrude","CAP_FACE",FACE,{"disambiguationData":[OSD([subQ3,subQ4,sQuery(id+"F2.wireOp",EDGE,"E91.sketch_text.stroke-0"),sQuery(id+"F2.wireOp",EDGE,"E91.sketch_text.stroke-1"),sQuery(id+"F2.wireOp",EDGE,"E91.sketch_text.stroke-2"),sQuery(id+"F2.wireOp",EDGE,"E91.sketch_text.stroke-3"),sQuery(id+"F2.wireOp",EDGE,"E91.sketch_text.stroke-4"),sQuery(id+"F2.wireOp",EDGE,"E91.sketch_text.stroke-5"),sQuery(id+"F2.wireOp",EDGE,"E91.sketch_text.stroke-6"),sQuery(id+"F2.wireOp",EDGE,"E91.sketch_text.stroke-7"),sQuery(id+"F2.wireOp",EDGE,"E91.sketch_text.stroke-8"),sQuery(id+"F2.wireOp",EDGE,"E91.sketch_text.stroke-10"),sQuery(id+"F2.wireOp",EDGE,"E91.sketch_text.stroke-11"),sQuery(id+"F2.wireOp",EDGE,"E91.sketch_text.stroke-13"),sQuery(id+"F2.wireOp",EDGE,"E91.sketch_text.stroke-14"),sQuery(id+"F2.wireOp",EDGE,"E91.sketch_text.stroke-15"),sQuery(id+"F2.wireOp",EDGE,"E91.sketch_text.stroke-17"),sQuery(id+"F2.wireOp",EDGE,"E91.sketch_text.stroke-18"),sQuery(id+"F2.wireOp",EDGE,"E91.sketch_text.stroke-19"),sQuery(id+"F2.wireOp",EDGE,"E91.sketch_text.stroke-20"),sQuery(id+"F2.wireOp",EDGE,"E91.sketch_text.stroke-21"),sQuery(id+"F2.wireOp",EDGE,"E91.sketch_text.stroke-22"),subQ1,subQ0,sQuery(id+"F2.wireOp",EDGE,"E91.sketch_text.stroke-25"),sQuery(id+"F2.wireOp",EDGE,"E91.sketch_text.stroke-26"),sQuery(id+"F2.wireOp",EDGE,"E91.sketch_text.stroke-27"),sQuery(id+"F2.wireOp",EDGE,"E91.sketch_text.stroke-28"),sQuery(id+"F2.wireOp",EDGE,"E91.sketch_text.stroke-29"),sQuery(id+"F2.wireOp",EDGE,"E91.sketch_text.stroke-30"),sQuery(id+"F2.wireOp",EDGE,"E91.sketch_text.stroke-31")])],"isStart":true})]})]}),makeQuery(id+"F14.opExtrude","CAP_FACE",FACE,{"disambiguationData":[OSD([subQ3,subQ2,subQ1,subQ0,sQuery(id+"F13.wireOp",EDGE,"E104.sketch_text.stroke-0"),sQuery(id+"F13.wireOp",EDGE,"E104.sketch_text.stroke-2"),sQuery(id+"F13.wireOp",EDGE,"E104.sketch_text.stroke-3"),sQuery(id+"F13.wireOp",EDGE,"E104.sketch_text.stroke-4"),sQuery(id+"F13.wireOp",EDGE,"E104.sketch_text.stroke-5"),sQuery(id+"F13.wireOp",EDGE,"E104.sketch_text.stroke-6"),sQuery(id+"F13.wireOp",EDGE,"E104.sketch_text.stroke-7"),sQuery(id+"F13.wireOp",EDGE,"E104.sketch_text.stroke-8")])],"isStart":true})]});}
            var sketch = newSketch(context, id + "F15", { "sketchPlane" : qUnion([Q0])});
            skText(sketch, "E105", { "text": "E", "fontName": "NotoSans-Bold.ttf"});
            const initialGuessF15  = {"E105": [0.01418, 0.0486, 0.17365, -0.9848, 0.022]};
            skSetInitialGuess(sketch, initialGuessF15);
            skSolve(sketch);
        }
        {
            var Q0;
            {var subQ17=sQuery(id+"F15.wireOp",EDGE,"E105.sketch_text.stroke-4");Q0=makeQuery(id+"F15.imprint","IMPRINT",FACE,{"disambiguationData":[TD([[makeQuery(id+"F15.imprint","IMPRINT",EDGE,{"derivedFrom":subQ17}),-1.0]])]});}
            var Q1;
            {var subQ0=sQuery(id+"F2.wireOp",EDGE,"E91.sketch_text.stroke-24");var subQ1=sQuery(id+"F2.wireOp",EDGE,"E91.sketch_text.stroke-23");var subQ2=sQuery(id+"F0.wireOp",EDGE,"E82.trimOffspring");var subQ3=sQuery(id+"F0.wireOp",EDGE,"E79.0");var subQ4=sQuery(id+"F0.wireOp",EDGE,"E80.0");var subQ5=sQuery(id+"F0.wireOp",EDGE,"E89.filletArc");var subQ6=sQuery(id+"F0.wireOp",EDGE,"E84");var subQ7=sQuery(id+"F0.wireOp",EDGE,"E83");Q1=makeQuery(id+"F14.boolean.opBoolean","MERGE",FACE,{"derivedFrom":[makeQuery(id+"F5.opBoolean","MERGE",FACE,{"derivedFrom":[makeQuery(id+"F3.opExtrude","CAP_FACE",FACE,{"disambiguationData":[OSD([subQ2,subQ7,subQ6,subQ5,sQuery(id+"F2.wireOp",EDGE,"E91.sketch_text.stroke-53"),sQuery(id+"F2.wireOp",EDGE,"E91.sketch_text.stroke-54"),sQuery(id+"F2.wireOp",EDGE,"E91.sketch_text.stroke-57"),sQuery(id+"F2.wireOp",EDGE,"E91.sketch_text.stroke-58"),sQuery(id+"F2.wireOp",EDGE,"E91.sketch_text.stroke-59"),sQuery(id+"F2.wireOp",EDGE,"E91.sketch_text.stroke-60"),sQuery(id+"F2.wireOp",EDGE,"E91.sketch_text.stroke-62"),sQuery(id+"F2.wireOp",EDGE,"E91.sketch_text.stroke-63"),sQuery(id+"F2.wireOp",EDGE,"E91.sketch_text.stroke-64"),sQuery(id+"F2.wireOp",EDGE,"E91.sketch_text.stroke-65"),sQuery(id+"F2.wireOp",EDGE,"E91.sketch_text.stroke-66"),sQuery(id+"F2.wireOp",EDGE,"E91.sketch_text.stroke-67"),sQuery(id+"F2.wireOp",EDGE,"E91.sketch_text.stroke-68"),sQuery(id+"F2.wireOp",EDGE,"E91.sketch_text.stroke-69"),sQuery(id+"F2.wireOp",EDGE,"E91.sketch_text.stroke-70"),sQuery(id+"F2.wireOp",EDGE,"E91.sketch_text.stroke-71")])],"isStart":false}),makeQuery(id+"F4.opBoolean","MERGE",FACE,{"derivedFrom":[makeQuery(id+"F1.opExtrude","CAP_FACE",FACE,{"disambiguationData":[OSD([sQuery(id+"F0.wireOp",EDGE,"E0"),sQuery(id+"F0.wireOp",EDGE,"E1"),sQuery(id+"F0.wireOp",EDGE,"E2"),sQuery(id+"F0.wireOp",EDGE,"E3"),sQuery(id+"F0.wireOp",EDGE,"E4"),sQuery(id+"F0.wireOp",EDGE,"E5"),sQuery(id+"F0.wireOp",EDGE,"E6"),sQuery(id+"F0.wireOp",EDGE,"E7"),sQuery(id+"F0.wireOp",EDGE,"E8"),sQuery(id+"F0.wireOp",EDGE,"E9"),sQuery(id+"F0.wireOp",EDGE,"E10"),sQuery(id+"F0.wireOp",EDGE,"E11"),sQuery(id+"F0.wireOp",EDGE,"E12"),sQuery(id+"F0.wireOp",EDGE,"E13"),sQuery(id+"F0.wireOp",EDGE,"E14"),sQuery(id+"F0.wireOp",EDGE,"E15"),sQuery(id+"F0.wireOp",EDGE,"E16"),sQuery(id+"F0.wireOp",EDGE,"E17"),sQuery(id+"F0.wireOp",EDGE,"E18"),sQuery(id+"F0.wireOp",EDGE,"E19"),sQuery(id+"F0.wireOp",EDGE,"E20"),sQuery(id+"F0.wireOp",EDGE,"E21"),sQuery(id+"F0.wireOp",EDGE,"E22"),sQuery(id+"F0.wireOp",EDGE,"E23"),sQuery(id+"F0.wireOp",EDGE,"E24"),sQuery(id+"F0.wireOp",EDGE,"E25"),sQuery(id+"F0.wireOp",EDGE,"E26"),sQuery(id+"F0.wireOp",EDGE,"E27"),sQuery(id+"F0.wireOp",EDGE,"E28"),sQuery(id+"F0.wireOp",EDGE,"E29"),sQuery(id+"F0.wireOp",EDGE,"E30"),sQuery(id+"F0.wireOp",EDGE,"E31"),sQuery(id+"F0.wireOp",EDGE,"E32"),sQuery(id+"F0.wireOp",EDGE,"E33"),sQuery(id+"F0.wireOp",EDGE,"E34"),sQuery(id+"F0.wireOp",EDGE,"E35"),sQuery(id+"F0.wireOp",EDGE,"E36"),sQuery(id+"F0.wireOp",EDGE,"E37"),sQuery(id+"F0.wireOp",EDGE,"E38"),sQuery(id+"F0.wireOp",EDGE,"E39"),sQuery(id+"F0.wireOp",EDGE,"E40"),sQuery(id+"F0.wireOp",EDGE,"E41"),sQuery(id+"F0.wireOp",EDGE,"E42"),sQuery(id+"F0.wireOp",EDGE,"E43"),sQuery(id+"F0.wireOp",EDGE,"E44"),sQuery(id+"F0.wireOp",EDGE,"E45"),sQuery(id+"F0.wireOp",EDGE,"E46"),sQuery(id+"F0.wireOp",EDGE,"E47"),sQuery(id+"F0.wireOp",EDGE,"E48"),sQuery(id+"F0.wireOp",EDGE,"E49"),sQuery(id+"F0.wireOp",EDGE,"E50"),sQuery(id+"F0.wireOp",EDGE,"E51"),sQuery(id+"F0.wireOp",EDGE,"E52"),sQuery(id+"F0.wireOp",EDGE,"E53"),sQuery(id+"F0.wireOp",EDGE,"E54"),sQuery(id+"F0.wireOp",EDGE,"E55"),sQuery(id+"F0.wireOp",EDGE,"E56"),sQuery(id+"F0.wireOp",EDGE,"E57"),sQuery(id+"F0.wireOp",EDGE,"E58"),sQuery(id+"F0.wireOp",EDGE,"E59"),sQuery(id+"F0.wireOp",EDGE,"E60"),sQuery(id+"F0.wireOp",EDGE,"E61"),sQuery(id+"F0.wireOp",EDGE,"E62"),sQuery(id+"F0.wireOp",EDGE,"E63"),sQuery(id+"F0.wireOp",EDGE,"E64"),sQuery(id+"F0.wireOp",EDGE,"E65"),sQuery(id+"F0.wireOp",EDGE,"E66"),sQuery(id+"F0.wireOp",EDGE,"E67"),sQuery(id+"F0.wireOp",EDGE,"E68"),sQuery(id+"F0.wireOp",EDGE,"E69"),sQuery(id+"F0.wireOp",EDGE,"E70"),sQuery(id+"F0.wireOp",EDGE,"E71"),sQuery(id+"F0.wireOp",EDGE,"E72"),sQuery(id+"F0.wireOp",EDGE,"E73"),sQuery(id+"F0.wireOp",EDGE,"E74"),sQuery(id+"F0.wireOp",EDGE,"E75"),sQuery(id+"F0.wireOp",EDGE,"E76"),sQuery(id+"F0.wireOp",EDGE,"E77"),sQuery(id+"F0.wireOp",EDGE,"E78"),subQ3,subQ4,sQuery(id+"F0.wireOp",EDGE,"E81.0"),subQ2,subQ7,subQ6,sQuery(id+"F0.wireOp",EDGE,"E85.filletArc"),sQuery(id+"F0.wireOp",EDGE,"E86.filletArc"),sQuery(id+"F0.wireOp",EDGE,"E87.filletArc"),sQuery(id+"F0.wireOp",EDGE,"E88.filletArc"),subQ5,sQuery(id+"F0.wireOp",EDGE,"E90.filletArc")])],"isStart":true}),makeQuery(id+"F3.opExtrude","CAP_FACE",FACE,{"disambiguationData":[OSD([subQ3,subQ4,sQuery(id+"F2.wireOp",EDGE,"E91.sketch_text.stroke-0"),sQuery(id+"F2.wireOp",EDGE,"E91.sketch_text.stroke-1"),sQuery(id+"F2.wireOp",EDGE,"E91.sketch_text.stroke-2"),sQuery(id+"F2.wireOp",EDGE,"E91.sketch_text.stroke-3"),sQuery(id+"F2.wireOp",EDGE,"E91.sketch_text.stroke-4"),sQuery(id+"F2.wireOp",EDGE,"E91.sketch_text.stroke-5"),sQuery(id+"F2.wireOp",EDGE,"E91.sketch_text.stroke-6"),sQuery(id+"F2.wireOp",EDGE,"E91.sketch_text.stroke-7"),sQuery(id+"F2.wireOp",EDGE,"E91.sketch_text.stroke-8"),sQuery(id+"F2.wireOp",EDGE,"E91.sketch_text.stroke-10"),sQuery(id+"F2.wireOp",EDGE,"E91.sketch_text.stroke-11"),sQuery(id+"F2.wireOp",EDGE,"E91.sketch_text.stroke-13"),sQuery(id+"F2.wireOp",EDGE,"E91.sketch_text.stroke-14"),sQuery(id+"F2.wireOp",EDGE,"E91.sketch_text.stroke-15"),sQuery(id+"F2.wireOp",EDGE,"E91.sketch_text.stroke-17"),sQuery(id+"F2.wireOp",EDGE,"E91.sketch_text.stroke-18"),sQuery(id+"F2.wireOp",EDGE,"E91.sketch_text.stroke-19"),sQuery(id+"F2.wireOp",EDGE,"E91.sketch_text.stroke-20"),sQuery(id+"F2.wireOp",EDGE,"E91.sketch_text.stroke-21"),sQuery(id+"F2.wireOp",EDGE,"E91.sketch_text.stroke-22"),subQ1,subQ0,sQuery(id+"F2.wireOp",EDGE,"E91.sketch_text.stroke-25"),sQuery(id+"F2.wireOp",EDGE,"E91.sketch_text.stroke-26"),sQuery(id+"F2.wireOp",EDGE,"E91.sketch_text.stroke-27"),sQuery(id+"F2.wireOp",EDGE,"E91.sketch_text.stroke-28"),sQuery(id+"F2.wireOp",EDGE,"E91.sketch_text.stroke-29"),sQuery(id+"F2.wireOp",EDGE,"E91.sketch_text.stroke-30"),sQuery(id+"F2.wireOp",EDGE,"E91.sketch_text.stroke-31")])],"isStart":false})]})]}),makeQuery(id+"F14.opExtrude","CAP_FACE",FACE,{"disambiguationData":[OSD([subQ3,subQ2,subQ1,subQ0,sQuery(id+"F13.wireOp",EDGE,"E104.sketch_text.stroke-0"),sQuery(id+"F13.wireOp",EDGE,"E104.sketch_text.stroke-2"),sQuery(id+"F13.wireOp",EDGE,"E104.sketch_text.stroke-3"),sQuery(id+"F13.wireOp",EDGE,"E104.sketch_text.stroke-4"),sQuery(id+"F13.wireOp",EDGE,"E104.sketch_text.stroke-5"),sQuery(id+"F13.wireOp",EDGE,"E104.sketch_text.stroke-6"),sQuery(id+"F13.wireOp",EDGE,"E104.sketch_text.stroke-7"),sQuery(id+"F13.wireOp",EDGE,"E104.sketch_text.stroke-8")])],"isStart":false})]});}
            extrude(context, id + "F16", {"entities" : qUnion([Q0]), "operationType" : NewBodyOperationType.ADD, "endBound" : BoundingType.UP_TO_SURFACE, "oppositeDirection" : true, "endBoundEntityFace" : qUnion([Q1]), "depth" : 25 * mm});
        }
        {
            var Q0;
            {var subQ0=sQuery(id+"F13.wireOp",EDGE,"E104.sketch_text.stroke-2");var subQ1=sQuery(id+"F2.wireOp",EDGE,"E91.sketch_text.stroke-59");var subQ2=sQuery(id+"F2.wireOp",EDGE,"E91.sketch_text.stroke-58");var subQ3=sQuery(id+"F0.wireOp",EDGE,"E84");var subQ4=sQuery(id+"F0.wireOp",EDGE,"E82.trimOffspring");var subQ5=sQuery(id+"F2.wireOp",EDGE,"E91.sketch_text.stroke-24");var subQ6=sQuery(id+"F2.wireOp",EDGE,"E91.sketch_text.stroke-23");var subQ7=sQuery(id+"F0.wireOp",EDGE,"E79.0");var subQ8=sQuery(id+"F0.wireOp",EDGE,"E80.0");var subQ9=sQuery(id+"F0.wireOp",EDGE,"E89.filletArc");var subQ10=sQuery(id+"F0.wireOp",EDGE,"E83");Q0=makeQuery(id+"F16.boolean.opBoolean","MERGE",FACE,{"derivedFrom":[makeQuery(id+"F14.boolean.opBoolean","MERGE",FACE,{"derivedFrom":[makeQuery(id+"F5.opBoolean","MERGE",FACE,{"derivedFrom":[makeQuery(id+"F3.opExtrude","CAP_FACE",FACE,{"disambiguationData":[OSD([subQ4,subQ10,subQ3,subQ9,sQuery(id+"F2.wireOp",EDGE,"E91.sketch_text.stroke-53"),sQuery(id+"F2.wireOp",EDGE,"E91.sketch_text.stroke-54"),sQuery(id+"F2.wireOp",EDGE,"E91.sketch_text.stroke-57"),subQ2,subQ1,sQuery(id+"F2.wireOp",EDGE,"E91.sketch_text.stroke-60"),sQuery(id+"F2.wireOp",EDGE,"E91.sketch_text.stroke-62"),sQuery(id+"F2.wireOp",EDGE,"E91.sketch_text.stroke-63"),sQuery(id+"F2.wireOp",EDGE,"E91.sketch_text.stroke-64"),sQuery(id+"F2.wireOp",EDGE,"E91.sketch_text.stroke-65"),sQuery(id+"F2.wireOp",EDGE,"E91.sketch_text.stroke-66"),sQuery(id+"F2.wireOp",EDGE,"E91.sketch_text.stroke-67"),sQuery(id+"F2.wireOp",EDGE,"E91.sketch_text.stroke-68"),sQuery(id+"F2.wireOp",EDGE,"E91.sketch_text.stroke-69"),sQuery(id+"F2.wireOp",EDGE,"E91.sketch_text.stroke-70"),sQuery(id+"F2.wireOp",EDGE,"E91.sketch_text.stroke-71")])],"isStart":true}),makeQuery(id+"F4.opBoolean","MERGE",FACE,{"derivedFrom":[makeQuery(id+"F1.opExtrude","CAP_FACE",FACE,{"disambiguationData":[OSD([sQuery(id+"F0.wireOp",EDGE,"E0"),sQuery(id+"F0.wireOp",EDGE,"E1"),sQuery(id+"F0.wireOp",EDGE,"E2"),sQuery(id+"F0.wireOp",EDGE,"E3"),sQuery(id+"F0.wireOp",EDGE,"E4"),sQuery(id+"F0.wireOp",EDGE,"E5"),sQuery(id+"F0.wireOp",EDGE,"E6"),sQuery(id+"F0.wireOp",EDGE,"E7"),sQuery(id+"F0.wireOp",EDGE,"E8"),sQuery(id+"F0.wireOp",EDGE,"E9"),sQuery(id+"F0.wireOp",EDGE,"E10"),sQuery(id+"F0.wireOp",EDGE,"E11"),sQuery(id+"F0.wireOp",EDGE,"E12"),sQuery(id+"F0.wireOp",EDGE,"E13"),sQuery(id+"F0.wireOp",EDGE,"E14"),sQuery(id+"F0.wireOp",EDGE,"E15"),sQuery(id+"F0.wireOp",EDGE,"E16"),sQuery(id+"F0.wireOp",EDGE,"E17"),sQuery(id+"F0.wireOp",EDGE,"E18"),sQuery(id+"F0.wireOp",EDGE,"E19"),sQuery(id+"F0.wireOp",EDGE,"E20"),sQuery(id+"F0.wireOp",EDGE,"E21"),sQuery(id+"F0.wireOp",EDGE,"E22"),sQuery(id+"F0.wireOp",EDGE,"E23"),sQuery(id+"F0.wireOp",EDGE,"E24"),sQuery(id+"F0.wireOp",EDGE,"E25"),sQuery(id+"F0.wireOp",EDGE,"E26"),sQuery(id+"F0.wireOp",EDGE,"E27"),sQuery(id+"F0.wireOp",EDGE,"E28"),sQuery(id+"F0.wireOp",EDGE,"E29"),sQuery(id+"F0.wireOp",EDGE,"E30"),sQuery(id+"F0.wireOp",EDGE,"E31"),sQuery(id+"F0.wireOp",EDGE,"E32"),sQuery(id+"F0.wireOp",EDGE,"E33"),sQuery(id+"F0.wireOp",EDGE,"E34"),sQuery(id+"F0.wireOp",EDGE,"E35"),sQuery(id+"F0.wireOp",EDGE,"E36"),sQuery(id+"F0.wireOp",EDGE,"E37"),sQuery(id+"F0.wireOp",EDGE,"E38"),sQuery(id+"F0.wireOp",EDGE,"E39"),sQuery(id+"F0.wireOp",EDGE,"E40"),sQuery(id+"F0.wireOp",EDGE,"E41"),sQuery(id+"F0.wireOp",EDGE,"E42"),sQuery(id+"F0.wireOp",EDGE,"E43"),sQuery(id+"F0.wireOp",EDGE,"E44"),sQuery(id+"F0.wireOp",EDGE,"E45"),sQuery(id+"F0.wireOp",EDGE,"E46"),sQuery(id+"F0.wireOp",EDGE,"E47"),sQuery(id+"F0.wireOp",EDGE,"E48"),sQuery(id+"F0.wireOp",EDGE,"E49"),sQuery(id+"F0.wireOp",EDGE,"E50"),sQuery(id+"F0.wireOp",EDGE,"E51"),sQuery(id+"F0.wireOp",EDGE,"E52"),sQuery(id+"F0.wireOp",EDGE,"E53"),sQuery(id+"F0.wireOp",EDGE,"E54"),sQuery(id+"F0.wireOp",EDGE,"E55"),sQuery(id+"F0.wireOp",EDGE,"E56"),sQuery(id+"F0.wireOp",EDGE,"E57"),sQuery(id+"F0.wireOp",EDGE,"E58"),sQuery(id+"F0.wireOp",EDGE,"E59"),sQuery(id+"F0.wireOp",EDGE,"E60"),sQuery(id+"F0.wireOp",EDGE,"E61"),sQuery(id+"F0.wireOp",EDGE,"E62"),sQuery(id+"F0.wireOp",EDGE,"E63"),sQuery(id+"F0.wireOp",EDGE,"E64"),sQuery(id+"F0.wireOp",EDGE,"E65"),sQuery(id+"F0.wireOp",EDGE,"E66"),sQuery(id+"F0.wireOp",EDGE,"E67"),sQuery(id+"F0.wireOp",EDGE,"E68"),sQuery(id+"F0.wireOp",EDGE,"E69"),sQuery(id+"F0.wireOp",EDGE,"E70"),sQuery(id+"F0.wireOp",EDGE,"E71"),sQuery(id+"F0.wireOp",EDGE,"E72"),sQuery(id+"F0.wireOp",EDGE,"E73"),sQuery(id+"F0.wireOp",EDGE,"E74"),sQuery(id+"F0.wireOp",EDGE,"E75"),sQuery(id+"F0.wireOp",EDGE,"E76"),sQuery(id+"F0.wireOp",EDGE,"E77"),sQuery(id+"F0.wireOp",EDGE,"E78"),subQ7,subQ8,sQuery(id+"F0.wireOp",EDGE,"E81.0"),subQ4,subQ10,subQ3,sQuery(id+"F0.wireOp",EDGE,"E85.filletArc"),sQuery(id+"F0.wireOp",EDGE,"E86.filletArc"),sQuery(id+"F0.wireOp",EDGE,"E87.filletArc"),sQuery(id+"F0.wireOp",EDGE,"E88.filletArc"),subQ9,sQuery(id+"F0.wireOp",EDGE,"E90.filletArc")])],"isStart":false}),makeQuery(id+"F3.opExtrude","CAP_FACE",FACE,{"disambiguationData":[OSD([subQ7,subQ8,sQuery(id+"F2.wireOp",EDGE,"E91.sketch_text.stroke-0"),sQuery(id+"F2.wireOp",EDGE,"E91.sketch_text.stroke-1"),sQuery(id+"F2.wireOp",EDGE,"E91.sketch_text.stroke-2"),sQuery(id+"F2.wireOp",EDGE,"E91.sketch_text.stroke-3"),sQuery(id+"F2.wireOp",EDGE,"E91.sketch_text.stroke-4"),sQuery(id+"F2.wireOp",EDGE,"E91.sketch_text.stroke-5"),sQuery(id+"F2.wireOp",EDGE,"E91.sketch_text.stroke-6"),sQuery(id+"F2.wireOp",EDGE,"E91.sketch_text.stroke-7"),sQuery(id+"F2.wireOp",EDGE,"E91.sketch_text.stroke-8"),sQuery(id+"F2.wireOp",EDGE,"E91.sketch_text.stroke-10"),sQuery(id+"F2.wireOp",EDGE,"E91.sketch_text.stroke-11"),sQuery(id+"F2.wireOp",EDGE,"E91.sketch_text.stroke-13"),sQuery(id+"F2.wireOp",EDGE,"E91.sketch_text.stroke-14"),sQuery(id+"F2.wireOp",EDGE,"E91.sketch_text.stroke-15"),sQuery(id+"F2.wireOp",EDGE,"E91.sketch_text.stroke-17"),sQuery(id+"F2.wireOp",EDGE,"E91.sketch_text.stroke-18"),sQuery(id+"F2.wireOp",EDGE,"E91.sketch_text.stroke-19"),sQuery(id+"F2.wireOp",EDGE,"E91.sketch_text.stroke-20"),sQuery(id+"F2.wireOp",EDGE,"E91.sketch_text.stroke-21"),sQuery(id+"F2.wireOp",EDGE,"E91.sketch_text.stroke-22"),subQ6,subQ5,sQuery(id+"F2.wireOp",EDGE,"E91.sketch_text.stroke-25"),sQuery(id+"F2.wireOp",EDGE,"E91.sketch_text.stroke-26"),sQuery(id+"F2.wireOp",EDGE,"E91.sketch_text.stroke-27"),sQuery(id+"F2.wireOp",EDGE,"E91.sketch_text.stroke-28"),sQuery(id+"F2.wireOp",EDGE,"E91.sketch_text.stroke-29"),sQuery(id+"F2.wireOp",EDGE,"E91.sketch_text.stroke-30"),sQuery(id+"F2.wireOp",EDGE,"E91.sketch_text.stroke-31")])],"isStart":true})]})]}),makeQuery(id+"F14.opExtrude","CAP_FACE",FACE,{"disambiguationData":[OSD([subQ7,subQ4,subQ6,subQ5,sQuery(id+"F13.wireOp",EDGE,"E104.sketch_text.stroke-0"),subQ0,sQuery(id+"F13.wireOp",EDGE,"E104.sketch_text.stroke-3"),sQuery(id+"F13.wireOp",EDGE,"E104.sketch_text.stroke-4"),sQuery(id+"F13.wireOp",EDGE,"E104.sketch_text.stroke-5"),sQuery(id+"F13.wireOp",EDGE,"E104.sketch_text.stroke-6"),sQuery(id+"F13.wireOp",EDGE,"E104.sketch_text.stroke-7"),sQuery(id+"F13.wireOp",EDGE,"E104.sketch_text.stroke-8")])],"isStart":true})]}),makeQuery(id+"F16.opExtrude","CAP_FACE",FACE,{"disambiguationData":[OSD([subQ4,subQ3,subQ2,subQ1,subQ0,sQuery(id+"F15.wireOp",EDGE,"E105.sketch_text.stroke-0"),sQuery(id+"F15.wireOp",EDGE,"E105.sketch_text.stroke-1"),sQuery(id+"F15.wireOp",EDGE,"E105.sketch_text.stroke-2"),sQuery(id+"F15.wireOp",EDGE,"E105.sketch_text.stroke-3"),sQuery(id+"F15.wireOp",EDGE,"E105.sketch_text.stroke-4"),sQuery(id+"F15.wireOp",EDGE,"E105.sketch_text.stroke-5"),sQuery(id+"F15.wireOp",EDGE,"E105.sketch_text.stroke-6"),sQuery(id+"F15.wireOp",EDGE,"E105.sketch_text.stroke-8"),sQuery(id+"F15.wireOp",EDGE,"E105.sketch_text.stroke-9"),sQuery(id+"F15.wireOp",EDGE,"E105.sketch_text.stroke-10"),sQuery(id+"F15.wireOp",EDGE,"E105.sketch_text.stroke-11")])],"isStart":true})]});}
            var sketch = newSketch(context, id + "F17", { "sketchPlane" : qUnion([Q0])});
            skLineSegment(sketch, "E106", {"start": v(12.94, 76.8) * mm, "end": v(39.85, 75.04) * mm, "construction": true});
            skArc(sketch, "E107", {"start": v(39.85, 75.04) * mm, "mid": v(27.27, 89.37) * mm, "end": v(12.94, 76.8) * mm});
            skArc(sketch, "E108.0", {"start": v(36.86, 75.24) * mm, "mid": v(27.08, 86.38) * mm, "end": v(15.94, 76.6) * mm});
            skFitSpline(sketch, "E109.0", {"points": [v(12.94, 76.8) * mm, v(21.77, 75.94) * mm, v(30.87, 75.4) * mm, v(39.85, 75.04) * mm]});
            skLineSegment(sketch, "E110", {"start": v(15.94, 76.6) * mm, "end": v(15.93, 76.52) * mm});
            skLineSegment(sketch, "E111", {"start": v(36.86, 75.24) * mm, "end": v(36.85, 75.17) * mm});
            skSolve(sketch);
        }
        {
            var Q0;
            {var subQ0=sQuery(id+"F13.wireOp",EDGE,"E104.sketch_text.stroke-2");var subQ1=sQuery(id+"F2.wireOp",EDGE,"E91.sketch_text.stroke-59");var subQ2=sQuery(id+"F2.wireOp",EDGE,"E91.sketch_text.stroke-58");var subQ3=sQuery(id+"F0.wireOp",EDGE,"E84");var subQ4=sQuery(id+"F0.wireOp",EDGE,"E82.trimOffspring");var subQ5=sQuery(id+"F2.wireOp",EDGE,"E91.sketch_text.stroke-24");var subQ6=sQuery(id+"F2.wireOp",EDGE,"E91.sketch_text.stroke-23");var subQ7=sQuery(id+"F0.wireOp",EDGE,"E79.0");var subQ8=sQuery(id+"F0.wireOp",EDGE,"E80.0");var subQ9=sQuery(id+"F0.wireOp",EDGE,"E89.filletArc");var subQ10=sQuery(id+"F0.wireOp",EDGE,"E83");Q0=makeQuery(id+"F16.boolean.opBoolean","MERGE",FACE,{"derivedFrom":[makeQuery(id+"F14.boolean.opBoolean","MERGE",FACE,{"derivedFrom":[makeQuery(id+"F5.opBoolean","MERGE",FACE,{"derivedFrom":[makeQuery(id+"F3.opExtrude","CAP_FACE",FACE,{"disambiguationData":[OSD([subQ4,subQ10,subQ3,subQ9,sQuery(id+"F2.wireOp",EDGE,"E91.sketch_text.stroke-53"),sQuery(id+"F2.wireOp",EDGE,"E91.sketch_text.stroke-54"),sQuery(id+"F2.wireOp",EDGE,"E91.sketch_text.stroke-57"),subQ2,subQ1,sQuery(id+"F2.wireOp",EDGE,"E91.sketch_text.stroke-60"),sQuery(id+"F2.wireOp",EDGE,"E91.sketch_text.stroke-62"),sQuery(id+"F2.wireOp",EDGE,"E91.sketch_text.stroke-63"),sQuery(id+"F2.wireOp",EDGE,"E91.sketch_text.stroke-64"),sQuery(id+"F2.wireOp",EDGE,"E91.sketch_text.stroke-65"),sQuery(id+"F2.wireOp",EDGE,"E91.sketch_text.stroke-66"),sQuery(id+"F2.wireOp",EDGE,"E91.sketch_text.stroke-67"),sQuery(id+"F2.wireOp",EDGE,"E91.sketch_text.stroke-68"),sQuery(id+"F2.wireOp",EDGE,"E91.sketch_text.stroke-69"),sQuery(id+"F2.wireOp",EDGE,"E91.sketch_text.stroke-70"),sQuery(id+"F2.wireOp",EDGE,"E91.sketch_text.stroke-71")])],"isStart":true}),makeQuery(id+"F4.opBoolean","MERGE",FACE,{"derivedFrom":[makeQuery(id+"F1.opExtrude","CAP_FACE",FACE,{"disambiguationData":[OSD([sQuery(id+"F0.wireOp",EDGE,"E0"),sQuery(id+"F0.wireOp",EDGE,"E1"),sQuery(id+"F0.wireOp",EDGE,"E2"),sQuery(id+"F0.wireOp",EDGE,"E3"),sQuery(id+"F0.wireOp",EDGE,"E4"),sQuery(id+"F0.wireOp",EDGE,"E5"),sQuery(id+"F0.wireOp",EDGE,"E6"),sQuery(id+"F0.wireOp",EDGE,"E7"),sQuery(id+"F0.wireOp",EDGE,"E8"),sQuery(id+"F0.wireOp",EDGE,"E9"),sQuery(id+"F0.wireOp",EDGE,"E10"),sQuery(id+"F0.wireOp",EDGE,"E11"),sQuery(id+"F0.wireOp",EDGE,"E12"),sQuery(id+"F0.wireOp",EDGE,"E13"),sQuery(id+"F0.wireOp",EDGE,"E14"),sQuery(id+"F0.wireOp",EDGE,"E15"),sQuery(id+"F0.wireOp",EDGE,"E16"),sQuery(id+"F0.wireOp",EDGE,"E17"),sQuery(id+"F0.wireOp",EDGE,"E18"),sQuery(id+"F0.wireOp",EDGE,"E19"),sQuery(id+"F0.wireOp",EDGE,"E20"),sQuery(id+"F0.wireOp",EDGE,"E21"),sQuery(id+"F0.wireOp",EDGE,"E22"),sQuery(id+"F0.wireOp",EDGE,"E23"),sQuery(id+"F0.wireOp",EDGE,"E24"),sQuery(id+"F0.wireOp",EDGE,"E25"),sQuery(id+"F0.wireOp",EDGE,"E26"),sQuery(id+"F0.wireOp",EDGE,"E27"),sQuery(id+"F0.wireOp",EDGE,"E28"),sQuery(id+"F0.wireOp",EDGE,"E29"),sQuery(id+"F0.wireOp",EDGE,"E30"),sQuery(id+"F0.wireOp",EDGE,"E31"),sQuery(id+"F0.wireOp",EDGE,"E32"),sQuery(id+"F0.wireOp",EDGE,"E33"),sQuery(id+"F0.wireOp",EDGE,"E34"),sQuery(id+"F0.wireOp",EDGE,"E35"),sQuery(id+"F0.wireOp",EDGE,"E36"),sQuery(id+"F0.wireOp",EDGE,"E37"),sQuery(id+"F0.wireOp",EDGE,"E38"),sQuery(id+"F0.wireOp",EDGE,"E39"),sQuery(id+"F0.wireOp",EDGE,"E40"),sQuery(id+"F0.wireOp",EDGE,"E41"),sQuery(id+"F0.wireOp",EDGE,"E42"),sQuery(id+"F0.wireOp",EDGE,"E43"),sQuery(id+"F0.wireOp",EDGE,"E44"),sQuery(id+"F0.wireOp",EDGE,"E45"),sQuery(id+"F0.wireOp",EDGE,"E46"),sQuery(id+"F0.wireOp",EDGE,"E47"),sQuery(id+"F0.wireOp",EDGE,"E48"),sQuery(id+"F0.wireOp",EDGE,"E49"),sQuery(id+"F0.wireOp",EDGE,"E50"),sQuery(id+"F0.wireOp",EDGE,"E51"),sQuery(id+"F0.wireOp",EDGE,"E52"),sQuery(id+"F0.wireOp",EDGE,"E53"),sQuery(id+"F0.wireOp",EDGE,"E54"),sQuery(id+"F0.wireOp",EDGE,"E55"),sQuery(id+"F0.wireOp",EDGE,"E56"),sQuery(id+"F0.wireOp",EDGE,"E57"),sQuery(id+"F0.wireOp",EDGE,"E58"),sQuery(id+"F0.wireOp",EDGE,"E59"),sQuery(id+"F0.wireOp",EDGE,"E60"),sQuery(id+"F0.wireOp",EDGE,"E61"),sQuery(id+"F0.wireOp",EDGE,"E62"),sQuery(id+"F0.wireOp",EDGE,"E63"),sQuery(id+"F0.wireOp",EDGE,"E64"),sQuery(id+"F0.wireOp",EDGE,"E65"),sQuery(id+"F0.wireOp",EDGE,"E66"),sQuery(id+"F0.wireOp",EDGE,"E67"),sQuery(id+"F0.wireOp",EDGE,"E68"),sQuery(id+"F0.wireOp",EDGE,"E69"),sQuery(id+"F0.wireOp",EDGE,"E70"),sQuery(id+"F0.wireOp",EDGE,"E71"),sQuery(id+"F0.wireOp",EDGE,"E72"),sQuery(id+"F0.wireOp",EDGE,"E73"),sQuery(id+"F0.wireOp",EDGE,"E74"),sQuery(id+"F0.wireOp",EDGE,"E75"),sQuery(id+"F0.wireOp",EDGE,"E76"),sQuery(id+"F0.wireOp",EDGE,"E77"),sQuery(id+"F0.wireOp",EDGE,"E78"),subQ7,subQ8,sQuery(id+"F0.wireOp",EDGE,"E81.0"),subQ4,subQ10,subQ3,sQuery(id+"F0.wireOp",EDGE,"E85.filletArc"),sQuery(id+"F0.wireOp",EDGE,"E86.filletArc"),sQuery(id+"F0.wireOp",EDGE,"E87.filletArc"),sQuery(id+"F0.wireOp",EDGE,"E88.filletArc"),subQ9,sQuery(id+"F0.wireOp",EDGE,"E90.filletArc")])],"isStart":false}),makeQuery(id+"F3.opExtrude","CAP_FACE",FACE,{"disambiguationData":[OSD([subQ7,subQ8,sQuery(id+"F2.wireOp",EDGE,"E91.sketch_text.stroke-0"),sQuery(id+"F2.wireOp",EDGE,"E91.sketch_text.stroke-1"),sQuery(id+"F2.wireOp",EDGE,"E91.sketch_text.stroke-2"),sQuery(id+"F2.wireOp",EDGE,"E91.sketch_text.stroke-3"),sQuery(id+"F2.wireOp",EDGE,"E91.sketch_text.stroke-4"),sQuery(id+"F2.wireOp",EDGE,"E91.sketch_text.stroke-5"),sQuery(id+"F2.wireOp",EDGE,"E91.sketch_text.stroke-6"),sQuery(id+"F2.wireOp",EDGE,"E91.sketch_text.stroke-7"),sQuery(id+"F2.wireOp",EDGE,"E91.sketch_text.stroke-8"),sQuery(id+"F2.wireOp",EDGE,"E91.sketch_text.stroke-10"),sQuery(id+"F2.wireOp",EDGE,"E91.sketch_text.stroke-11"),sQuery(id+"F2.wireOp",EDGE,"E91.sketch_text.stroke-13"),sQuery(id+"F2.wireOp",EDGE,"E91.sketch_text.stroke-14"),sQuery(id+"F2.wireOp",EDGE,"E91.sketch_text.stroke-15"),sQuery(id+"F2.wireOp",EDGE,"E91.sketch_text.stroke-17"),sQuery(id+"F2.wireOp",EDGE,"E91.sketch_text.stroke-18"),sQuery(id+"F2.wireOp",EDGE,"E91.sketch_text.stroke-19"),sQuery(id+"F2.wireOp",EDGE,"E91.sketch_text.stroke-20"),sQuery(id+"F2.wireOp",EDGE,"E91.sketch_text.stroke-21"),sQuery(id+"F2.wireOp",EDGE,"E91.sketch_text.stroke-22"),subQ6,subQ5,sQuery(id+"F2.wireOp",EDGE,"E91.sketch_text.stroke-25"),sQuery(id+"F2.wireOp",EDGE,"E91.sketch_text.stroke-26"),sQuery(id+"F2.wireOp",EDGE,"E91.sketch_text.stroke-27"),sQuery(id+"F2.wireOp",EDGE,"E91.sketch_text.stroke-28"),sQuery(id+"F2.wireOp",EDGE,"E91.sketch_text.stroke-29"),sQuery(id+"F2.wireOp",EDGE,"E91.sketch_text.stroke-30"),sQuery(id+"F2.wireOp",EDGE,"E91.sketch_text.stroke-31")])],"isStart":true})]})]}),makeQuery(id+"F14.opExtrude","CAP_FACE",FACE,{"disambiguationData":[OSD([subQ7,subQ4,subQ6,subQ5,sQuery(id+"F13.wireOp",EDGE,"E104.sketch_text.stroke-0"),subQ0,sQuery(id+"F13.wireOp",EDGE,"E104.sketch_text.stroke-3"),sQuery(id+"F13.wireOp",EDGE,"E104.sketch_text.stroke-4"),sQuery(id+"F13.wireOp",EDGE,"E104.sketch_text.stroke-5"),sQuery(id+"F13.wireOp",EDGE,"E104.sketch_text.stroke-6"),sQuery(id+"F13.wireOp",EDGE,"E104.sketch_text.stroke-7"),sQuery(id+"F13.wireOp",EDGE,"E104.sketch_text.stroke-8")])],"isStart":true})]}),makeQuery(id+"F16.opExtrude","CAP_FACE",FACE,{"disambiguationData":[OSD([subQ4,subQ3,subQ2,subQ1,subQ0,sQuery(id+"F15.wireOp",EDGE,"E105.sketch_text.stroke-0"),sQuery(id+"F15.wireOp",EDGE,"E105.sketch_text.stroke-1"),sQuery(id+"F15.wireOp",EDGE,"E105.sketch_text.stroke-2"),sQuery(id+"F15.wireOp",EDGE,"E105.sketch_text.stroke-3"),sQuery(id+"F15.wireOp",EDGE,"E105.sketch_text.stroke-4"),sQuery(id+"F15.wireOp",EDGE,"E105.sketch_text.stroke-5"),sQuery(id+"F15.wireOp",EDGE,"E105.sketch_text.stroke-6"),sQuery(id+"F15.wireOp",EDGE,"E105.sketch_text.stroke-8"),sQuery(id+"F15.wireOp",EDGE,"E105.sketch_text.stroke-9"),sQuery(id+"F15.wireOp",EDGE,"E105.sketch_text.stroke-10"),sQuery(id+"F15.wireOp",EDGE,"E105.sketch_text.stroke-11")])],"isStart":true})]});}
            var sketch = newSketch(context, id + "F18", { "sketchPlane" : qUnion([Q0])});
            skFitSpline(sketch, "E112.0.0", {"points": [v(39.85, 75.04) * mm, v(30.87, 75.4) * mm, v(21.77, 75.94) * mm, v(12.94, 76.8) * mm]});
            skLineSegment(sketch, "E112.0.1", {"start": v(12.94, 76.8) * mm, "end": v(7.68, 44.1) * mm});
            skLineSegment(sketch, "E112.0.2", {"start": v(7.68, 44.1) * mm, "end": v(8.75, 43.35) * mm});
            skLineSegment(sketch, "E112.0.3", {"start": v(8.75, 43.35) * mm, "end": v(7.97, 43.35) * mm});
            skLineSegment(sketch, "E112.0.4", {"start": v(7.97, 43.35) * mm, "end": v(7.97, 42.17) * mm});
            skLineSegment(sketch, "E112.0.5", {"start": v(7.97, 42.17) * mm, "end": v(10.17, 39.93) * mm});
            skLineSegment(sketch, "E112.0.6", {"start": v(10.17, 39.93) * mm, "end": v(10.74, 40.49) * mm});
            skLineSegment(sketch, "E112.0.7", {"start": v(10.74, 40.49) * mm, "end": v(11.19, 40.03) * mm});
            skLineSegment(sketch, "E112.0.8", {"start": v(11.19, 40.03) * mm, "end": v(11, 39.57) * mm});
            skLineSegment(sketch, "E112.0.9", {"start": v(11, 39.57) * mm, "end": v(11.46, 39.39) * mm});
            skLineSegment(sketch, "E112.0.10", {"start": v(11.46, 39.39) * mm, "end": v(11.46, 38.73) * mm});
            skLineSegment(sketch, "E112.0.11", {"start": v(11.46, 38.73) * mm, "end": v(12.08, 38.61) * mm});
            skLineSegment(sketch, "E112.0.12", {"start": v(12.08, 38.61) * mm, "end": v(12.08, 37.96) * mm});
            skLineSegment(sketch, "E112.0.13", {"start": v(12.08, 37.96) * mm, "end": v(12.25, 37.87) * mm});
            skLineSegment(sketch, "E112.0.14", {"start": v(12.25, 37.87) * mm, "end": v(12.46, 37.8) * mm});
            skLineSegment(sketch, "E112.0.15", {"start": v(12.46, 37.8) * mm, "end": v(12.46, 37.52) * mm});
            skLineSegment(sketch, "E112.0.16", {"start": v(12.46, 37.52) * mm, "end": v(12.25, 37.52) * mm});
            skLineSegment(sketch, "E112.0.17", {"start": v(12.25, 37.52) * mm, "end": v(12.25, 36.96) * mm});
            skLineSegment(sketch, "E112.0.18", {"start": v(12.25, 36.96) * mm, "end": v(12.43, 36.93) * mm});
            skLineSegment(sketch, "E112.0.19", {"start": v(12.43, 36.93) * mm, "end": v(12.75, 36.55) * mm});
            skLineSegment(sketch, "E112.0.20", {"start": v(12.75, 36.55) * mm, "end": v(12.75, 36.3) * mm});
            skLineSegment(sketch, "E112.0.21", {"start": v(12.75, 36.3) * mm, "end": v(12.46, 36.3) * mm});
            skLineSegment(sketch, "E112.0.22", {"start": v(12.46, 36.3) * mm, "end": v(12.46, 35.94) * mm});
            skLineSegment(sketch, "E112.0.23", {"start": v(12.46, 35.94) * mm, "end": v(13.34, 35.94) * mm});
            skLineSegment(sketch, "E112.0.24", {"start": v(13.34, 35.94) * mm, "end": v(13.45, 36.34) * mm});
            skLineSegment(sketch, "E112.0.25", {"start": v(13.45, 36.34) * mm, "end": v(14.19, 35.72) * mm});
            skLineSegment(sketch, "E112.0.26", {"start": v(14.19, 35.72) * mm, "end": v(13.73, 35.19) * mm});
            skLineSegment(sketch, "E112.0.27", {"start": v(13.73, 35.19) * mm, "end": v(13.79, 34.75) * mm});
            skLineSegment(sketch, "E112.0.28", {"start": v(13.79, 34.75) * mm, "end": v(14.47, 34.2) * mm});
            skLineSegment(sketch, "E112.0.29", {"start": v(14.47, 34.2) * mm, "end": v(15.28, 34.2) * mm});
            skLineSegment(sketch, "E112.0.30", {"start": v(15.28, 34.2) * mm, "end": v(15.28, 33.54) * mm});
            skLineSegment(sketch, "E112.0.31", {"start": v(15.28, 33.54) * mm, "end": v(15.46, 33.54) * mm});
            skLineSegment(sketch, "E112.0.32", {"start": v(15.46, 33.54) * mm, "end": v(15.46, 33.22) * mm});
            skLineSegment(sketch, "E112.0.33", {"start": v(15.46, 33.22) * mm, "end": v(15.87, 33.22) * mm});
            skLineSegment(sketch, "E112.0.34", {"start": v(15.87, 33.22) * mm, "end": v(16.14, 32.43) * mm});
            skLineSegment(sketch, "E112.0.35", {"start": v(16.14, 32.43) * mm, "end": v(16.14, 31.7) * mm});
            skLineSegment(sketch, "E112.0.36", {"start": v(16.14, 31.7) * mm, "end": v(16.97, 31.7) * mm});
            skLineSegment(sketch, "E112.0.37", {"start": v(16.97, 31.7) * mm, "end": v(17.27, 32.23) * mm});
            skLineSegment(sketch, "E112.0.38", {"start": v(17.27, 32.23) * mm, "end": v(17.33, 31.74) * mm});
            skLineSegment(sketch, "E112.0.39", {"start": v(17.33, 31.74) * mm, "end": v(17.48, 31.65) * mm});
            skLineSegment(sketch, "E112.0.40", {"start": v(17.48, 31.65) * mm, "end": v(17.48, 31.25) * mm});
            skLineSegment(sketch, "E112.0.41", {"start": v(17.48, 31.25) * mm, "end": v(17.7, 31.18) * mm});
            skLineSegment(sketch, "E112.0.42", {"start": v(17.7, 31.18) * mm, "end": v(17.7, 30.7) * mm});
            skLineSegment(sketch, "E112.0.43", {"start": v(17.7, 30.7) * mm, "end": v(18.01, 30.66) * mm});
            skLineSegment(sketch, "E112.0.44", {"start": v(18.01, 30.66) * mm, "end": v(18.01, 30.29) * mm});
            skLineSegment(sketch, "E112.0.45", {"start": v(18.01, 30.29) * mm, "end": v(18.18, 30.2) * mm});
            skLineSegment(sketch, "E112.0.46", {"start": v(18.18, 30.2) * mm, "end": v(18.33, 30.17) * mm});
            skLineSegment(sketch, "E112.0.47", {"start": v(18.33, 30.17) * mm, "end": v(18.33, 29.33) * mm});
            skLineSegment(sketch, "E112.0.48", {"start": v(18.33, 29.33) * mm, "end": v(18.46, 29) * mm});
            skLineSegment(sketch, "E112.0.49", {"start": v(18.46, 29) * mm, "end": v(18.83, 27.8) * mm});
            skLineSegment(sketch, "E112.0.50", {"start": v(18.83, 27.8) * mm, "end": v(20, 27.8) * mm});
            skLineSegment(sketch, "E112.0.51", {"start": v(20, 27.8) * mm, "end": v(20, 27.5) * mm});
            skLineSegment(sketch, "E112.0.52", {"start": v(20, 27.5) * mm, "end": v(20.36, 27.3) * mm});
            skLineSegment(sketch, "E112.0.53", {"start": v(20.36, 27.3) * mm, "end": v(20.36, 26.6) * mm});
            skLineSegment(sketch, "E112.0.54", {"start": v(20.36, 26.6) * mm, "end": v(21.15, 25.9) * mm});
            skLineSegment(sketch, "E112.0.55", {"start": v(21.15, 25.9) * mm, "end": v(21.45, 25.9) * mm});
            skLineSegment(sketch, "E112.0.56", {"start": v(21.45, 25.9) * mm, "end": v(21.5, 25.75) * mm});
            skLineSegment(sketch, "E112.0.57", {"start": v(21.5, 25.75) * mm, "end": v(21.21, 25.6) * mm});
            skLineSegment(sketch, "E112.0.58", {"start": v(21.21, 25.6) * mm, "end": v(21.3, 25.31) * mm});
            skLineSegment(sketch, "E112.0.59", {"start": v(21.3, 25.31) * mm, "end": v(21.54, 25.28) * mm});
            skLineSegment(sketch, "E112.0.60", {"start": v(21.54, 25.28) * mm, "end": v(21.6, 24.78) * mm});
            skLineSegment(sketch, "E112.0.61", {"start": v(21.6, 24.78) * mm, "end": v(21.94, 24.82) * mm});
            skLineSegment(sketch, "E112.0.62", {"start": v(21.94, 24.82) * mm, "end": v(21.99, 25.2) * mm});
            skLineSegment(sketch, "E112.0.63", {"start": v(21.99, 25.2) * mm, "end": v(22.33, 25.1) * mm});
            skLineSegment(sketch, "E112.0.64", {"start": v(22.33, 25.1) * mm, "end": v(22.84, 23.96) * mm});
            skLineSegment(sketch, "E112.0.65", {"start": v(22.84, 23.96) * mm, "end": v(23.05, 23.94) * mm});
            skLineSegment(sketch, "E112.0.66", {"start": v(23.05, 23.94) * mm, "end": v(23.05, 20.17) * mm});
            skLineSegment(sketch, "E112.0.67", {"start": v(23.05, 20.17) * mm, "end": v(22.65, 19.46) * mm});
            skLineSegment(sketch, "E112.0.68", {"start": v(22.65, 19.46) * mm, "end": v(22.95, 18.48) * mm});
            skLineSegment(sketch, "E112.0.69", {"start": v(22.95, 18.48) * mm, "end": v(23.56, 18.23) * mm});
            skLineSegment(sketch, "E112.0.70", {"start": v(23.56, 18.23) * mm, "end": v(23.64, 17.74) * mm});
            skLineSegment(sketch, "E112.0.71", {"start": v(23.64, 17.74) * mm, "end": v(24.27, 17.22) * mm});
            skLineSegment(sketch, "E112.0.72", {"start": v(24.27, 17.22) * mm, "end": v(24.63, 17.14) * mm});
            skLineSegment(sketch, "E112.0.73", {"start": v(24.63, 17.14) * mm, "end": v(24.72, 16.67) * mm});
            skLineSegment(sketch, "E112.0.74", {"start": v(24.72, 16.67) * mm, "end": v(24.9, 16.57) * mm});
            skLineSegment(sketch, "E112.0.75", {"start": v(24.9, 16.57) * mm, "end": v(24.9, 16.14) * mm});
            skLineSegment(sketch, "E112.0.76", {"start": v(24.9, 16.14) * mm, "end": v(39.85, 15.87) * mm});
            skLineSegment(sketch, "E112.0.77", {"start": v(39.85, 15.87) * mm, "end": v(39.85, 75.04) * mm});
            skLineSegment(sketch, "E113.0", {"start": v(15.31, 72.63) * mm, "end": v(15.13, 71.54) * mm});
            skLineSegment(sketch, "E114.0", {"start": v(36.85, 54.14) * mm, "end": v(36.85, 71.2) * mm});
            skLineSegment(sketch, "E115", {"start": v(15.31, 72.63) * mm, "end": v(15.94, 76.52) * mm});
            skLineSegment(sketch, "E116", {"start": v(36.85, 71.2) * mm, "end": v(36.85, 75.17) * mm});
            skLineSegment(sketch, "E117", {"start": v(15.94, 76.52) * mm, "end": v(36.85, 75.17) * mm, "construction": true});
            skArc(sketch, "E118", {"start": v(36.85, 75.17) * mm, "mid": v(27.07, 86.3) * mm, "end": v(15.94, 76.52) * mm});
            skArc(sketch, "E119.0", {"start": v(33.86, 75.38) * mm, "mid": v(26.87, 83.3) * mm, "end": v(18.93, 76.33) * mm});
            skFitSpline(sketch, "E120.0", {"points": [v(12.94, 76.8) * mm, v(21.77, 75.94) * mm, v(30.87, 75.4) * mm, v(39.85, 75.04) * mm]});
            skFitSpline(sketch, "E121.0", {"points": [v(12.94, 76.8) * mm, v(21.77, 75.94) * mm, v(30.87, 75.4) * mm, v(39.85, 75.04) * mm]});
            skLineSegment(sketch, "E122", {"start": v(33.86, 75.38) * mm, "end": v(33.85, 75.3) * mm});
            skSolve(sketch);
        }
        {
            var Q0;
            Q0=makeQuery(id+"F18.imprint","IMPRINT",FACE,{"disambiguationData":[TD([[makeQuery(id+"F18.imprint","IMPRINT",EDGE,{"derivedFrom":sQuery(id+"F18.wireOp",EDGE,"E118")}),1.0]])]});
            var Q1;
            {var subQ0=sQuery(id+"F13.wireOp",EDGE,"E104.sketch_text.stroke-2");var subQ1=sQuery(id+"F2.wireOp",EDGE,"E91.sketch_text.stroke-59");var subQ2=sQuery(id+"F2.wireOp",EDGE,"E91.sketch_text.stroke-58");var subQ3=sQuery(id+"F0.wireOp",EDGE,"E84");var subQ4=sQuery(id+"F0.wireOp",EDGE,"E82.trimOffspring");var subQ5=sQuery(id+"F2.wireOp",EDGE,"E91.sketch_text.stroke-24");var subQ6=sQuery(id+"F2.wireOp",EDGE,"E91.sketch_text.stroke-23");var subQ7=sQuery(id+"F0.wireOp",EDGE,"E79.0");var subQ8=sQuery(id+"F0.wireOp",EDGE,"E80.0");var subQ9=sQuery(id+"F0.wireOp",EDGE,"E89.filletArc");var subQ10=sQuery(id+"F0.wireOp",EDGE,"E83");Q1=makeQuery(id+"F16.boolean.opBoolean","MERGE",FACE,{"derivedFrom":[makeQuery(id+"F14.boolean.opBoolean","MERGE",FACE,{"derivedFrom":[makeQuery(id+"F5.opBoolean","MERGE",FACE,{"derivedFrom":[makeQuery(id+"F3.opExtrude","CAP_FACE",FACE,{"disambiguationData":[OSD([subQ4,subQ10,subQ3,subQ9,sQuery(id+"F2.wireOp",EDGE,"E91.sketch_text.stroke-53"),sQuery(id+"F2.wireOp",EDGE,"E91.sketch_text.stroke-54"),sQuery(id+"F2.wireOp",EDGE,"E91.sketch_text.stroke-57"),subQ2,subQ1,sQuery(id+"F2.wireOp",EDGE,"E91.sketch_text.stroke-60"),sQuery(id+"F2.wireOp",EDGE,"E91.sketch_text.stroke-62"),sQuery(id+"F2.wireOp",EDGE,"E91.sketch_text.stroke-63"),sQuery(id+"F2.wireOp",EDGE,"E91.sketch_text.stroke-64"),sQuery(id+"F2.wireOp",EDGE,"E91.sketch_text.stroke-65"),sQuery(id+"F2.wireOp",EDGE,"E91.sketch_text.stroke-66"),sQuery(id+"F2.wireOp",EDGE,"E91.sketch_text.stroke-67"),sQuery(id+"F2.wireOp",EDGE,"E91.sketch_text.stroke-68"),sQuery(id+"F2.wireOp",EDGE,"E91.sketch_text.stroke-69"),sQuery(id+"F2.wireOp",EDGE,"E91.sketch_text.stroke-70"),sQuery(id+"F2.wireOp",EDGE,"E91.sketch_text.stroke-71")])],"isStart":false}),makeQuery(id+"F4.opBoolean","MERGE",FACE,{"derivedFrom":[makeQuery(id+"F1.opExtrude","CAP_FACE",FACE,{"disambiguationData":[OSD([sQuery(id+"F0.wireOp",EDGE,"E0"),sQuery(id+"F0.wireOp",EDGE,"E1"),sQuery(id+"F0.wireOp",EDGE,"E2"),sQuery(id+"F0.wireOp",EDGE,"E3"),sQuery(id+"F0.wireOp",EDGE,"E4"),sQuery(id+"F0.wireOp",EDGE,"E5"),sQuery(id+"F0.wireOp",EDGE,"E6"),sQuery(id+"F0.wireOp",EDGE,"E7"),sQuery(id+"F0.wireOp",EDGE,"E8"),sQuery(id+"F0.wireOp",EDGE,"E9"),sQuery(id+"F0.wireOp",EDGE,"E10"),sQuery(id+"F0.wireOp",EDGE,"E11"),sQuery(id+"F0.wireOp",EDGE,"E12"),sQuery(id+"F0.wireOp",EDGE,"E13"),sQuery(id+"F0.wireOp",EDGE,"E14"),sQuery(id+"F0.wireOp",EDGE,"E15"),sQuery(id+"F0.wireOp",EDGE,"E16"),sQuery(id+"F0.wireOp",EDGE,"E17"),sQuery(id+"F0.wireOp",EDGE,"E18"),sQuery(id+"F0.wireOp",EDGE,"E19"),sQuery(id+"F0.wireOp",EDGE,"E20"),sQuery(id+"F0.wireOp",EDGE,"E21"),sQuery(id+"F0.wireOp",EDGE,"E22"),sQuery(id+"F0.wireOp",EDGE,"E23"),sQuery(id+"F0.wireOp",EDGE,"E24"),sQuery(id+"F0.wireOp",EDGE,"E25"),sQuery(id+"F0.wireOp",EDGE,"E26"),sQuery(id+"F0.wireOp",EDGE,"E27"),sQuery(id+"F0.wireOp",EDGE,"E28"),sQuery(id+"F0.wireOp",EDGE,"E29"),sQuery(id+"F0.wireOp",EDGE,"E30"),sQuery(id+"F0.wireOp",EDGE,"E31"),sQuery(id+"F0.wireOp",EDGE,"E32"),sQuery(id+"F0.wireOp",EDGE,"E33"),sQuery(id+"F0.wireOp",EDGE,"E34"),sQuery(id+"F0.wireOp",EDGE,"E35"),sQuery(id+"F0.wireOp",EDGE,"E36"),sQuery(id+"F0.wireOp",EDGE,"E37"),sQuery(id+"F0.wireOp",EDGE,"E38"),sQuery(id+"F0.wireOp",EDGE,"E39"),sQuery(id+"F0.wireOp",EDGE,"E40"),sQuery(id+"F0.wireOp",EDGE,"E41"),sQuery(id+"F0.wireOp",EDGE,"E42"),sQuery(id+"F0.wireOp",EDGE,"E43"),sQuery(id+"F0.wireOp",EDGE,"E44"),sQuery(id+"F0.wireOp",EDGE,"E45"),sQuery(id+"F0.wireOp",EDGE,"E46"),sQuery(id+"F0.wireOp",EDGE,"E47"),sQuery(id+"F0.wireOp",EDGE,"E48"),sQuery(id+"F0.wireOp",EDGE,"E49"),sQuery(id+"F0.wireOp",EDGE,"E50"),sQuery(id+"F0.wireOp",EDGE,"E51"),sQuery(id+"F0.wireOp",EDGE,"E52"),sQuery(id+"F0.wireOp",EDGE,"E53"),sQuery(id+"F0.wireOp",EDGE,"E54"),sQuery(id+"F0.wireOp",EDGE,"E55"),sQuery(id+"F0.wireOp",EDGE,"E56"),sQuery(id+"F0.wireOp",EDGE,"E57"),sQuery(id+"F0.wireOp",EDGE,"E58"),sQuery(id+"F0.wireOp",EDGE,"E59"),sQuery(id+"F0.wireOp",EDGE,"E60"),sQuery(id+"F0.wireOp",EDGE,"E61"),sQuery(id+"F0.wireOp",EDGE,"E62"),sQuery(id+"F0.wireOp",EDGE,"E63"),sQuery(id+"F0.wireOp",EDGE,"E64"),sQuery(id+"F0.wireOp",EDGE,"E65"),sQuery(id+"F0.wireOp",EDGE,"E66"),sQuery(id+"F0.wireOp",EDGE,"E67"),sQuery(id+"F0.wireOp",EDGE,"E68"),sQuery(id+"F0.wireOp",EDGE,"E69"),sQuery(id+"F0.wireOp",EDGE,"E70"),sQuery(id+"F0.wireOp",EDGE,"E71"),sQuery(id+"F0.wireOp",EDGE,"E72"),sQuery(id+"F0.wireOp",EDGE,"E73"),sQuery(id+"F0.wireOp",EDGE,"E74"),sQuery(id+"F0.wireOp",EDGE,"E75"),sQuery(id+"F0.wireOp",EDGE,"E76"),sQuery(id+"F0.wireOp",EDGE,"E77"),sQuery(id+"F0.wireOp",EDGE,"E78"),subQ7,subQ8,sQuery(id+"F0.wireOp",EDGE,"E81.0"),subQ4,subQ10,subQ3,sQuery(id+"F0.wireOp",EDGE,"E85.filletArc"),sQuery(id+"F0.wireOp",EDGE,"E86.filletArc"),sQuery(id+"F0.wireOp",EDGE,"E87.filletArc"),sQuery(id+"F0.wireOp",EDGE,"E88.filletArc"),subQ9,sQuery(id+"F0.wireOp",EDGE,"E90.filletArc")])],"isStart":true}),makeQuery(id+"F3.opExtrude","CAP_FACE",FACE,{"disambiguationData":[OSD([subQ7,subQ8,sQuery(id+"F2.wireOp",EDGE,"E91.sketch_text.stroke-0"),sQuery(id+"F2.wireOp",EDGE,"E91.sketch_text.stroke-1"),sQuery(id+"F2.wireOp",EDGE,"E91.sketch_text.stroke-2"),sQuery(id+"F2.wireOp",EDGE,"E91.sketch_text.stroke-3"),sQuery(id+"F2.wireOp",EDGE,"E91.sketch_text.stroke-4"),sQuery(id+"F2.wireOp",EDGE,"E91.sketch_text.stroke-5"),sQuery(id+"F2.wireOp",EDGE,"E91.sketch_text.stroke-6"),sQuery(id+"F2.wireOp",EDGE,"E91.sketch_text.stroke-7"),sQuery(id+"F2.wireOp",EDGE,"E91.sketch_text.stroke-8"),sQuery(id+"F2.wireOp",EDGE,"E91.sketch_text.stroke-10"),sQuery(id+"F2.wireOp",EDGE,"E91.sketch_text.stroke-11"),sQuery(id+"F2.wireOp",EDGE,"E91.sketch_text.stroke-13"),sQuery(id+"F2.wireOp",EDGE,"E91.sketch_text.stroke-14"),sQuery(id+"F2.wireOp",EDGE,"E91.sketch_text.stroke-15"),sQuery(id+"F2.wireOp",EDGE,"E91.sketch_text.stroke-17"),sQuery(id+"F2.wireOp",EDGE,"E91.sketch_text.stroke-18"),sQuery(id+"F2.wireOp",EDGE,"E91.sketch_text.stroke-19"),sQuery(id+"F2.wireOp",EDGE,"E91.sketch_text.stroke-20"),sQuery(id+"F2.wireOp",EDGE,"E91.sketch_text.stroke-21"),sQuery(id+"F2.wireOp",EDGE,"E91.sketch_text.stroke-22"),subQ6,subQ5,sQuery(id+"F2.wireOp",EDGE,"E91.sketch_text.stroke-25"),sQuery(id+"F2.wireOp",EDGE,"E91.sketch_text.stroke-26"),sQuery(id+"F2.wireOp",EDGE,"E91.sketch_text.stroke-27"),sQuery(id+"F2.wireOp",EDGE,"E91.sketch_text.stroke-28"),sQuery(id+"F2.wireOp",EDGE,"E91.sketch_text.stroke-29"),sQuery(id+"F2.wireOp",EDGE,"E91.sketch_text.stroke-30"),sQuery(id+"F2.wireOp",EDGE,"E91.sketch_text.stroke-31")])],"isStart":false})]})]}),makeQuery(id+"F14.opExtrude","CAP_FACE",FACE,{"disambiguationData":[OSD([subQ7,subQ4,subQ6,subQ5,sQuery(id+"F13.wireOp",EDGE,"E104.sketch_text.stroke-0"),subQ0,sQuery(id+"F13.wireOp",EDGE,"E104.sketch_text.stroke-3"),sQuery(id+"F13.wireOp",EDGE,"E104.sketch_text.stroke-4"),sQuery(id+"F13.wireOp",EDGE,"E104.sketch_text.stroke-5"),sQuery(id+"F13.wireOp",EDGE,"E104.sketch_text.stroke-6"),sQuery(id+"F13.wireOp",EDGE,"E104.sketch_text.stroke-7"),sQuery(id+"F13.wireOp",EDGE,"E104.sketch_text.stroke-8")])],"isStart":false})]}),makeQuery(id+"F16.opExtrude","CAP_FACE",FACE,{"disambiguationData":[OSD([subQ4,subQ3,subQ2,subQ1,subQ0,sQuery(id+"F15.wireOp",EDGE,"E105.sketch_text.stroke-0"),sQuery(id+"F15.wireOp",EDGE,"E105.sketch_text.stroke-1"),sQuery(id+"F15.wireOp",EDGE,"E105.sketch_text.stroke-2"),sQuery(id+"F15.wireOp",EDGE,"E105.sketch_text.stroke-3"),sQuery(id+"F15.wireOp",EDGE,"E105.sketch_text.stroke-4"),sQuery(id+"F15.wireOp",EDGE,"E105.sketch_text.stroke-5"),sQuery(id+"F15.wireOp",EDGE,"E105.sketch_text.stroke-6"),sQuery(id+"F15.wireOp",EDGE,"E105.sketch_text.stroke-8"),sQuery(id+"F15.wireOp",EDGE,"E105.sketch_text.stroke-9"),sQuery(id+"F15.wireOp",EDGE,"E105.sketch_text.stroke-10"),sQuery(id+"F15.wireOp",EDGE,"E105.sketch_text.stroke-11")])],"isStart":false})]});}
            extrude(context, id + "F19", {"entities" : qUnion([Q0]), "endBound" : BoundingType.UP_TO_SURFACE, "oppositeDirection" : true, "endBoundEntityFace" : qUnion([Q1]), "depth" : 25 * mm});
        }
        {
            var Q0;
            Q0=makeQuery(id+"F19.opExtrude","CAP_FACE",FACE,{"disambiguationData":[OSD([sQuery(id+"F18.wireOp",EDGE,"E118"),sQuery(id+"F18.wireOp",EDGE,"E121.0")])],"isStart":true});
            var sketch = newSketch(context, id + "F20", { "sketchPlane" : qUnion([Q0])});
            skArc(sketch, "E123.0", {"start": v(36.85, 75.17) * mm, "mid": v(27.07, 86.3) * mm, "end": v(15.94, 76.52) * mm});
            skCircle(sketch, "E124", {"center": v(26.4, 75.84) * mm, "radius": 7.48 * mm});
            skFitSpline(sketch, "E125.0", {"points": [v(12.94, 76.8) * mm, v(21.77, 75.94) * mm, v(30.87, 75.4) * mm, v(39.85, 75.04) * mm]});
            skSolve(sketch);
        }
        {
            var Q0;
            {var subQ0=sQuery(id+"F20.wireOp",EDGE,"E125.0");var subQ1=sQuery(id+"F20.wireOp",EDGE,"E124");var subQ2=makeQuery(id+"F20.imprint","INTERSECT",VERTEX,{"disambiguationData":[OD(0.0)],"derivedFrom":[subQ1,subQ0]});Q0=makeQuery(id+"F20.imprint","IMPRINT",FACE,{"disambiguationData":[TD([[makeQuery(id+"F20.imprint","IMPRINT",EDGE,{"disambiguationData":[TD([[subQ2,1.0]])],"derivedFrom":subQ1}),1.0]])]});}
            extrude(context, id + "F21", {"entities" : qUnion([Q0]), "operationType" : NewBodyOperationType.REMOVE, "oppositeDirection" : true, "depth" : 25 * mm});
        }
        {
            var Q0;
            Q0=makeQuery(id+"F21.boolean.opBoolean","COPY",EDGE,{"derivedFrom":makeQuery(id+"F21.opExtrude","CAP_EDGE",EDGE,{"disambiguationData":[OSD([sQuery(id+"F20.wireOp",EDGE,"E124")])],"isStart":true})});
            var Q1;
            Q1=makeQuery(id+"F21.boolean.opBoolean","INTERSECT",EDGE,{"derivedFrom":[makeQuery(id+"F19.opExtrude","CAP_FACE",FACE,{"disambiguationData":[OSD([sQuery(id+"F18.wireOp",EDGE,"E118"),sQuery(id+"F18.wireOp",EDGE,"E121.0")])],"isStart":false}),makeQuery(id+"F21.opExtrude","SWEPT_FACE",FACE,{"disambiguationData":[OSD([sQuery(id+"F20.wireOp",EDGE,"E124")])]})]});
            var Q2;
            Q2=makeQuery(id+"F19.opExtrude","CAP_EDGE",EDGE,{"disambiguationData":[OSD([sQuery(id+"F18.wireOp",EDGE,"E118")])],"isStart":false});
            var Q3;
            Q3=makeQuery(id+"F19.opExtrude","CAP_EDGE",EDGE,{"disambiguationData":[OSD([sQuery(id+"F18.wireOp",EDGE,"E118")])],"isStart":true});
            var Q4;
            {var subQ0=sQuery(id+"F18.wireOp",EDGE,"E121.0");var subQ1=sQuery(id+"F18.wireOp",EDGE,"E118");Q4=makeQuery(id+"F19.opExtrude","SWEPT_EDGE",EDGE,{"disambiguationData":[OSD([subQ1,subQ0]),TDD([makeQuery(id+"F18.imprint","INTERSECT",VERTEX,{"disambiguationData":[OD(0.0)],"derivedFrom":[subQ1,subQ0]})])]});}
            var Q5;
            {var subQ0=sQuery(id+"F20.wireOp",EDGE,"E125.0");var subQ1=sQuery(id+"F20.wireOp",EDGE,"E124");Q5=makeQuery(id+"F21.boolean.opBoolean","COPY",EDGE,{"derivedFrom":makeQuery(id+"F21.opExtrude","SWEPT_EDGE",EDGE,{"disambiguationData":[OSD([subQ1,subQ0]),TDD([makeQuery(id+"F20.imprint","INTERSECT",VERTEX,{"disambiguationData":[OD(0.0)],"derivedFrom":[subQ1,subQ0]})])]})});}
            var Q6;
            {var subQ0=sQuery(id+"F20.wireOp",EDGE,"E125.0");var subQ1=sQuery(id+"F20.wireOp",EDGE,"E124");Q6=makeQuery(id+"F21.boolean.opBoolean","COPY",EDGE,{"derivedFrom":makeQuery(id+"F21.opExtrude","SWEPT_EDGE",EDGE,{"disambiguationData":[OSD([subQ1,subQ0]),TDD([makeQuery(id+"F20.imprint","INTERSECT",VERTEX,{"disambiguationData":[OD(1.0)],"derivedFrom":[subQ1,subQ0]})])]})});}
            var Q7;
            {var subQ0=sQuery(id+"F18.wireOp",EDGE,"E121.0");var subQ1=sQuery(id+"F18.wireOp",EDGE,"E118");Q7=makeQuery(id+"F19.opExtrude","SWEPT_EDGE",EDGE,{"disambiguationData":[OSD([subQ1,subQ0]),TDD([makeQuery(id+"F18.imprint","INTERSECT",VERTEX,{"disambiguationData":[OD(1.0)],"derivedFrom":[subQ1,subQ0]})])]});}
            fillet(context, id + "F22", {"entities" : qUnion([Q0, Q1, Q2, Q3, Q4, Q5, Q6, Q7]), "radius" : 1.5 * mm, "tangentPropagation" : true, "allowEdgeOverflow" : false});
        }
    });
